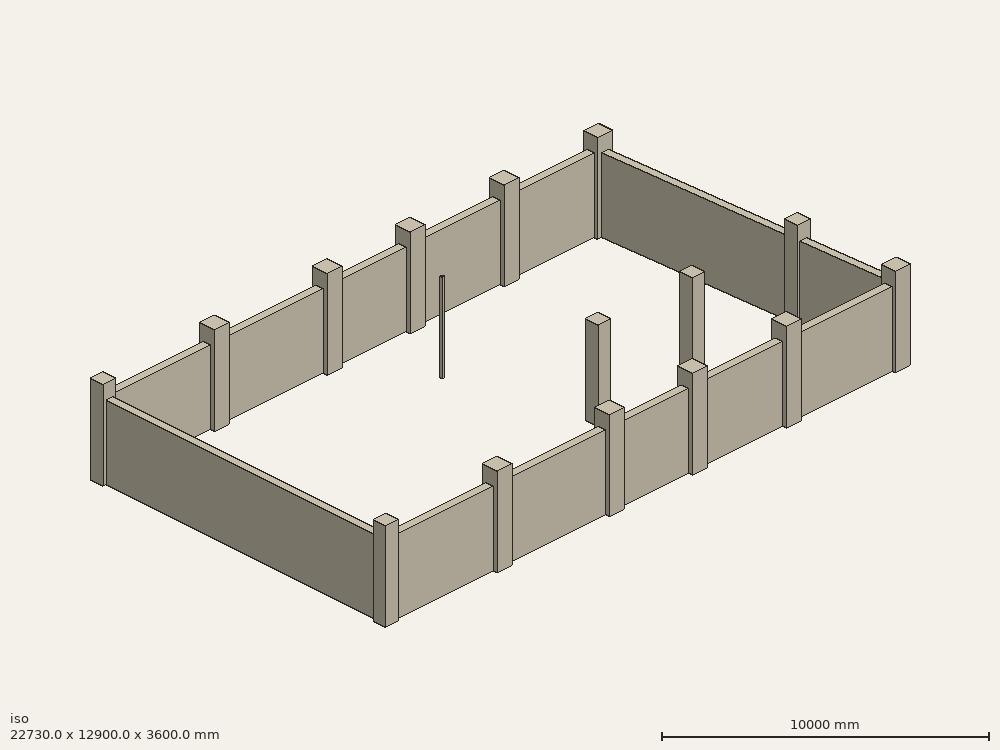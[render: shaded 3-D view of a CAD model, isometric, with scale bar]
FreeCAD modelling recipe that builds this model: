
FCSTD DOCUMENT  (FreeCAD 0.19R24291 (Git))
Label: karimi
License: All rights reserved
LicenseURL: http://en.wikipedia.org/wiki/All_rights_reserved
objects: App::FeaturePython×115, Part::Part2DObjectPython×66, Part::FeaturePython×45, Part::Feature×20, App::DocumentObjectGroup×5, App::DocumentObjectGroupPython×2, App::MaterialObjectPython×1, Fem::ConstraintForce×1
note: 260 computed .brp shape members not serialized (recipe doc carries the construction recipe); baked Part::Feature solids carry a one-line shape summary decoded from their .brp

FEATURE [App::DocumentObjectGroup] Columns
FEATURE [Part::Part2DObjectPython] C65X65_20T25_C40  label="C65X65-20T25_C40"  # Draft 2D object (typed FeaturePython)
  Height = 650
  Width = 650
FEATURE [Part::Part2DObjectPython] C65X65_16T20_C40  label="C65X65-16T20_C40"  # Draft 2D object (typed FeaturePython)
  Height = 650
  Width = 650
FEATURE [Part::Part2DObjectPython] C65X65_16T25_C40  label="C65X65-16T25_C40"  # Draft 2D object (typed FeaturePython)
  Height = 650
  Width = 650
FEATURE [Part::Part2DObjectPython] C55X55_12T25_C40  label="C55X55-12T25_C40"  # Draft 2D object (typed FeaturePython)
  Height = 550
  Width = 550
FEATURE [Part::Part2DObjectPython] C55X55_20T25_C40  label="C55X55-20T25_C40"  # Draft 2D object (typed FeaturePython)
  Height = 550
  Width = 550
FEATURE [Part::Part2DObjectPython] Line026  # Draft 2D object (typed FeaturePython)
  Area = 0
  ChamferSize = 0
  Closed = false
  End = (4790,12260,0)
  FilletRadius = 0
  Length = 12250
  MakeFace = true
  Points = (2) [(4790,10,0),(4790,12260,0)]
  Start = (4790,10,0)
  Subdivisions = 0
  type = Beam
FEATURE [Part::Part2DObjectPython] Line027  # Draft 2D object (typed FeaturePython)
  Area = 0
  ChamferSize = 0
  Closed = false
  End = (21910,4110,0)
  FilletRadius = 0
  Length = 4570
  MakeFace = true
  Points = (2) [(17340,4110,0),(21910,4110,0)]
  Start = (17340,4110,0)
  Subdivisions = 0
  type = Beam
FEATURE [Part::Part2DObjectPython] Line028  # Draft 2D object (typed FeaturePython)
  Area = 0
  ChamferSize = 0
  Closed = false
  End = (17340,4110,0)
  FilletRadius = 0
  Length = 4080
  MakeFace = true
  Points = (2) [(13260,4110,0),(17340,4110,0)]
  Start = (13260,4110,0)
  Subdivisions = 0
  type = Beam
FEATURE [Part::Part2DObjectPython] Line035  # Draft 2D object (typed FeaturePython)
  Area = 0
  ChamferSize = 0
  Closed = false
  End = (9660,12260,0)
  FilletRadius = 0
  Length = 12250
  MakeFace = true
  Points = (2) [(9660,10,0),(9660,12260,0)]
  Start = (9660,10,0)
  Subdivisions = 0
  type = Beam
FEATURE [Part::Part2DObjectPython] Line036  # Draft 2D object (typed FeaturePython)
  Area = 0
  ChamferSize = 0
  Closed = false
  End = (13260,4110,0)
  FilletRadius = 0
  Length = 3600
  MakeFace = true
  Points = (2) [(9660,4110,0),(13260,4110,0)]
  Start = (9660,4110,0)
  Subdivisions = 0
  type = Beam
FEATURE [App::DocumentObjectGroup] Beams
  Group = -> [Line026,Line027,Line028,Line035,Line036]
FEATURE [Part::Part2DObjectPython] BOX10X10  # Draft 2D object (typed FeaturePython)
  Height = 100
  Thickness = 4
  Width = 100
FEATURE [App::FeaturePython] Safe  # WARN: FeaturePython — macro-defined, semantics opaque (R4)
  input = <path>
  input_str = <blob: 95420 chars omitted>
  output = <path>
FEATURE [Part::Part2DObjectPython] Line037  # Draft 2D object (typed FeaturePython)
  Area = 0
  ChamferSize = 0
  Closed = false
  End = (13260,10,0)
  FilletRadius = 0
  Length = 12250
  MakeFace = true
  Points = (2) [(13260,12260,0),(13260,10,0)]
  Start = (13260,12260,0)
  Subdivisions = 0
  type = Beam
FEATURE [Part::Part2DObjectPython] Line038  # Draft 2D object (typed FeaturePython)
  Area = 0
  ChamferSize = 0
  Closed = false
  End = (17340,10,0)
  FilletRadius = 0
  Length = 12250
  MakeFace = true
  Points = (2) [(17340,12260,0),(17340,10,0)]
  Start = (17340,12260,0)
  Subdivisions = 0
  type = Beam
FEATURE [App::FeaturePython] Layer001  label="DIM"  # WARN: FeaturePython — macro-defined, semantics opaque (R4)
FEATURE [App::FeaturePython] Layer002  label="text"  # WARN: FeaturePython — macro-defined, semantics opaque (R4)
FEATURE [App::FeaturePython] Layer003  label="Defpoints"  # WARN: FeaturePython — macro-defined, semantics opaque (R4)
FEATURE [App::FeaturePython] Layer004  label="1"  # WARN: FeaturePython — macro-defined, semantics opaque (R4)
FEATURE [App::FeaturePython] Layer005  label="2"  # WARN: FeaturePython — macro-defined, semantics opaque (R4)
FEATURE [App::FeaturePython] Layer006  label="Furniture"  # WARN: FeaturePython — macro-defined, semantics opaque (R4)
FEATURE [App::FeaturePython] Layer007  label="M"  # WARN: FeaturePython — macro-defined, semantics opaque (R4)
FEATURE [App::FeaturePython] Layer008  label="11"  # WARN: FeaturePython — macro-defined, semantics opaque (R4)
FEATURE [App::FeaturePython] Layer009  label="WALL"  # WARN: FeaturePython — macro-defined, semantics opaque (R4)
FEATURE [App::FeaturePython] Layer010  label="TX"  # WARN: FeaturePython — macro-defined, semantics opaque (R4)
FEATURE [App::FeaturePython] Layer011  label="8"  # WARN: FeaturePython — macro-defined, semantics opaque (R4)
FEATURE [App::FeaturePython] Layer012  label="D"  # WARN: FeaturePython — macro-defined, semantics opaque (R4)
FEATURE [App::FeaturePython] Layer013  label="DIM1"  # WARN: FeaturePython — macro-defined, semantics opaque (R4)
FEATURE [App::FeaturePython] Layer014  label="moble1"  # WARN: FeaturePython — macro-defined, semantics opaque (R4)
FEATURE [App::FeaturePython] Layer015  label="sazeh"  # WARN: FeaturePython — macro-defined, semantics opaque (R4)
FEATURE [App::FeaturePython] Layer016  label="kadr"  # WARN: FeaturePython — macro-defined, semantics opaque (R4)
FEATURE [App::FeaturePython] Layer017  label="3"  # WARN: FeaturePython — macro-defined, semantics opaque (R4)
FEATURE [App::FeaturePython] Layer018  label="$AUDIT-BAD-LAYER"  # WARN: FeaturePython — macro-defined, semantics opaque (R4)
FEATURE [App::FeaturePython] Layer019  label="HS2"  # WARN: FeaturePython — macro-defined, semantics opaque (R4)
FEATURE [App::FeaturePython] Layer020  label="t"  # WARN: FeaturePython — macro-defined, semantics opaque (R4)
FEATURE [App::FeaturePython] Layer021  label="LAYER1"  # WARN: FeaturePython — macro-defined, semantics opaque (R4)
FEATURE [App::FeaturePython] Layer022  label="TXT"  # WARN: FeaturePython — macro-defined, semantics opaque (R4)
FEATURE [App::FeaturePython] Layer023  label="CADR"  # WARN: FeaturePython — macro-defined, semantics opaque (R4)
FEATURE [App::FeaturePython] Layer024  label="Kk"  # WARN: FeaturePython — macro-defined, semantics opaque (R4)
FEATURE [App::FeaturePython] Layer025  label="AR"  # WARN: FeaturePython — macro-defined, semantics opaque (R4)
FEATURE [App::FeaturePython] Layer026  label="kader"  # WARN: FeaturePython — macro-defined, semantics opaque (R4)
FEATURE [App::FeaturePython] Layer027  label="Ar-1"  # WARN: FeaturePython — macro-defined, semantics opaque (R4)
FEATURE [App::FeaturePython] Layer028  label="A-CADRE"  # WARN: FeaturePython — macro-defined, semantics opaque (R4)
FEATURE [App::FeaturePython] Layer029  label="TEXT - 0"  # WARN: FeaturePython — macro-defined, semantics opaque (R4)
FEATURE [App::FeaturePython] Layer030  label="band 3"  # WARN: FeaturePython — macro-defined, semantics opaque (R4)
FEATURE [App::FeaturePython] Layer031  label="PP"  # WARN: FeaturePython — macro-defined, semantics opaque (R4)
FEATURE [App::FeaturePython] Layer032  label="DOOR"  # WARN: FeaturePython — macro-defined, semantics opaque (R4)
FEATURE [App::FeaturePython] Layer033  label="PELEH"  # WARN: FeaturePython — macro-defined, semantics opaque (R4)
FEATURE [App::FeaturePython] Layer034  label="AXE"  # WARN: FeaturePython — macro-defined, semantics opaque (R4)
FEATURE [App::FeaturePython] Layer035  label="HATCH"  # WARN: FeaturePython — macro-defined, semantics opaque (R4)
FEATURE [App::FeaturePython] Layer036  label="DI"  # WARN: FeaturePython — macro-defined, semantics opaque (R4)
FEATURE [App::FeaturePython] Layer037  label="FUR"  # WARN: FeaturePython — macro-defined, semantics opaque (R4)
FEATURE [App::FeaturePython] Layer038  label="HID"  # WARN: FeaturePython — macro-defined, semantics opaque (R4)
FEATURE [App::FeaturePython] Layer039  label="Kit"  # WARN: FeaturePython — macro-defined, semantics opaque (R4)
FEATURE [App::FeaturePython] Layer040  label="win"  # WARN: FeaturePython — macro-defined, semantics opaque (R4)
FEATURE [App::FeaturePython] Layer041  label="HA-WALL"  # WARN: FeaturePython — macro-defined, semantics opaque (R4)
FEATURE [App::FeaturePython] Layer042  label="col2"  # WARN: FeaturePython — macro-defined, semantics opaque (R4)
FEATURE [App::FeaturePython] Layer043  label="DOOR-H"  # WARN: FeaturePython — macro-defined, semantics opaque (R4)
FEATURE [App::FeaturePython] Layer044  label="Stair"  # WARN: FeaturePython — macro-defined, semantics opaque (R4)
FEATURE [App::FeaturePython] Layer045  label="air curtain"  # WARN: FeaturePython — macro-defined, semantics opaque (R4)
FEATURE [App::FeaturePython] Layer046  label="tk"  # WARN: FeaturePython — macro-defined, semantics opaque (R4)
FEATURE [App::FeaturePython] Layer047  label="HIDDEN"  # WARN: FeaturePython — macro-defined, semantics opaque (R4)
FEATURE [App::FeaturePython] Layer049  label="A-DIM-AXIS"  # WARN: FeaturePython — macro-defined, semantics opaque (R4)
FEATURE [App::FeaturePython] Layer050  label="fur1"  # WARN: FeaturePython — macro-defined, semantics opaque (R4)
FEATURE [App::FeaturePython] Layer051  label="MOBL"  # WARN: FeaturePython — macro-defined, semantics opaque (R4)
FEATURE [App::FeaturePython] Layer052  label="W"  # WARN: FeaturePython — macro-defined, semantics opaque (R4)
FEATURE [App::FeaturePython] Layer053  label="H"  # WARN: FeaturePython — macro-defined, semantics opaque (R4)
FEATURE [App::FeaturePython] Layer054  label="FF"  # WARN: FeaturePython — macro-defined, semantics opaque (R4)
FEATURE [App::FeaturePython] Layer055  label="FL"  # WARN: FeaturePython — macro-defined, semantics opaque (R4)
FEATURE [App::FeaturePython] Layer056  label="7"  # WARN: FeaturePython — macro-defined, semantics opaque (R4)
FEATURE [App::FeaturePython] Layer057  label="1."  # WARN: FeaturePython — macro-defined, semantics opaque (R4)
FEATURE [App::FeaturePython] Layer058  label="2."  # WARN: FeaturePython — macro-defined, semantics opaque (R4)
FEATURE [App::FeaturePython] Layer059  label="AM_0"  # WARN: FeaturePython — macro-defined, semantics opaque (R4)
FEATURE [App::FeaturePython] Layer060  label="A-PROFILE"  # WARN: FeaturePython — macro-defined, semantics opaque (R4)
FEATURE [App::FeaturePython] Layer061  label="A-DOOR"  # WARN: FeaturePython — macro-defined, semantics opaque (R4)
FEATURE [App::FeaturePython] Layer062  label="A-STAIR"  # WARN: FeaturePython — macro-defined, semantics opaque (R4)
FEATURE [App::FeaturePython] Layer063  label="WINDOW"  # WARN: FeaturePython — macro-defined, semantics opaque (R4)
FEATURE [App::FeaturePython] Layer064  label="PUERTAS"  # WARN: FeaturePython — macro-defined, semantics opaque (R4)
FEATURE [App::FeaturePython] Layer065  label="FURN"  # WARN: FeaturePython — macro-defined, semantics opaque (R4)
FEATURE [App::FeaturePython] Layer066  label="251"  # WARN: FeaturePython — macro-defined, semantics opaque (R4)
FEATURE [App::FeaturePython] Layer067  label="FURNITURE-SERVICE"  # WARN: FeaturePython — macro-defined, semantics opaque (R4)
FEATURE [App::FeaturePython] Layer068  label="NO PRINT"  # WARN: FeaturePython — macro-defined, semantics opaque (R4)
FEATURE [App::FeaturePython] Layer069  label="67"  # WARN: FeaturePython — macro-defined, semantics opaque (R4)
FEATURE [App::FeaturePython] Layer070  label="mobleman .1"  # WARN: FeaturePython — macro-defined, semantics opaque (R4)
FEATURE [App::FeaturePython] Layer071  label="Frame"  # WARN: FeaturePython — macro-defined, semantics opaque (R4)
FEATURE [App::FeaturePython] Layer072  label="carros"  # WARN: FeaturePython — macro-defined, semantics opaque (R4)
FEATURE [App::FeaturePython] Layer073  label="MUEBLES"  # WARN: FeaturePython — macro-defined, semantics opaque (R4)
FEATURE [App::FeaturePython] Layer074  label="NOI THAT"  # WARN: FeaturePython — macro-defined, semantics opaque (R4)
FEATURE [App::FeaturePython] Layer075  label="B-FURNITURE"  # WARN: FeaturePython — macro-defined, semantics opaque (R4)
FEATURE [App::FeaturePython] Layer076  label="nazok kary"  # WARN: FeaturePython — macro-defined, semantics opaque (R4)
FEATURE [App::FeaturePython] Layer077  label="mobiliarios"  # WARN: FeaturePython — macro-defined, semantics opaque (R4)
FEATURE [App::FeaturePython] Layer078  label="moveis"  # WARN: FeaturePython — macro-defined, semantics opaque (R4)
FEATURE [App::FeaturePython] Layer079  label="PLANTAS"  # WARN: FeaturePython — macro-defined, semantics opaque (R4)
FEATURE [App::FeaturePython] Layer080  label="PROIEZIONI"  # WARN: FeaturePython — macro-defined, semantics opaque (R4)
FEATURE [App::FeaturePython] Layer081  label="NEMA"  # WARN: FeaturePython — macro-defined, semantics opaque (R4)
FEATURE [App::FeaturePython] Layer082  label="facade"  # WARN: FeaturePython — macro-defined, semantics opaque (R4)
FEATURE [App::FeaturePython] Layer083  label="khat chin"  # WARN: FeaturePython — macro-defined, semantics opaque (R4)
FEATURE [App::FeaturePython] Layer084  label="A-FURNITURE"  # WARN: FeaturePython — macro-defined, semantics opaque (R4)
FEATURE [App::FeaturePython] Layer085  label="NIVO"  # WARN: FeaturePython — macro-defined, semantics opaque (R4)
FEATURE [App::FeaturePython] Layer086  label="ext-wall"  # WARN: FeaturePython — macro-defined, semantics opaque (R4)
FEATURE [App::FeaturePython] Layer087  label="stairs"  # WARN: FeaturePython — macro-defined, semantics opaque (R4)
FEATURE [App::FeaturePython] Layer088  label="Plot-TEXT-2"  # WARN: FeaturePython — macro-defined, semantics opaque (R4)
FEATURE [App::FeaturePython] Layer089  label="A-AXIS"  # WARN: FeaturePython — macro-defined, semantics opaque (R4)
FEATURE [App::FeaturePython] Layer090  label="int-wall"  # WARN: FeaturePython — macro-defined, semantics opaque (R4)
FEATURE [App::FeaturePython] Layer091  label="STAIR2"  # WARN: FeaturePython — macro-defined, semantics opaque (R4)
FEATURE [App::FeaturePython] Layer092  label="kadr 2"  # WARN: FeaturePython — macro-defined, semantics opaque (R4)
FEATURE [App::FeaturePython] Layer093  label="WIN FACAD"  # WARN: FeaturePython — macro-defined, semantics opaque (R4)
FEATURE [App::FeaturePython] Layer094  label="win1"  # WARN: FeaturePython — macro-defined, semantics opaque (R4)
FEATURE [App::FeaturePython] Layer095  label="javab5"  # WARN: FeaturePython — macro-defined, semantics opaque (R4)
FEATURE [App::FeaturePython] Layer096  label="99"  # WARN: FeaturePython — macro-defined, semantics opaque (R4)
FEATURE [App::FeaturePython] Layer097  label="A-SECTION"  # WARN: FeaturePython — macro-defined, semantics opaque (R4)
FEATURE [App::FeaturePython] Layer098  label="a"  # WARN: FeaturePython — macro-defined, semantics opaque (R4)
FEATURE [Part::Feature] Line039
  shape: bbox 5774 x 11470 x 2e-07 mm, 0 faces, 0 solids (baked)
FEATURE [App::FeaturePython] Layer048  label="A-WALL"  # WARN: FeaturePython — macro-defined, semantics opaque (R4)
  Group = -> [Line039]
FEATURE [Part::Feature] Line040
  shape: bbox 22090 x 2e-07 x 2e-07 mm, 0 faces, 0 solids (baked)
FEATURE [Part::Feature] Line041
  shape: bbox 710 x 13000 x 2e-07 mm, 0 faces, 0 solids (baked)
FEATURE [Part::Feature] Line042
  shape: bbox 22800 x 2e-07 x 2e-07 mm, 0 faces, 0 solids (baked)
FEATURE [Part::Feature] Line043
  shape: bbox 2e-07 x 13000 x 2e-07 mm, 0 faces, 0 solids (baked)
FEATURE [Part::Feature] Block_fghfhfhg
  Placement = pos=(21402.7,12250,0) rot=(0,0,1;0rad)
  shape: bbox 875 x 875 x 2e-07 mm, 2 faces, 0 solids (baked)
FEATURE [Part::Feature] Block_fghfhfhg001
  Placement = pos=(9650,12250,0) rot=(0,0,1;0rad)
  shape: bbox 875 x 875 x 2e-07 mm, 2 faces, 0 solids (baked)
FEATURE [Part::Feature] Block_fghfhfhg002
  Placement = pos=(13250,12250,0) rot=(0,0,1;0rad)
  shape: bbox 875 x 875 x 2e-07 mm, 2 faces, 0 solids (baked)
FEATURE [Part::Feature] Block_fghfhfhg003
  Placement = pos=(17326.4,12250,0) rot=(0,0,1;0rad)
  shape: bbox 875 x 875 x 2e-07 mm, 2 faces, 0 solids (baked)
FEATURE [Part::Feature] Block_fghfhfhg004
  Placement = pos=(22071.6,0,0) rot=(0,0,1;0rad)
  shape: bbox 875 x 875 x 2e-07 mm, 2 faces, 0 solids (baked)
FEATURE [Part::Feature] Block_fghfhfhg005
  Placement = pos=(21898.8,4100,0) rot=(0,0,1;0rad)
  shape: bbox 875 x 875 x 2e-07 mm, 2 faces, 0 solids (baked)
FEATURE [Part::Feature] Block_fghfhfhg006
  Placement = pos=(17324.6,4100,0) rot=(0,0,1;0rad)
  shape: bbox 875 x 875 x 2e-07 mm, 2 faces, 0 solids (baked)
FEATURE [Part::Feature] Block_fghfhfhg007
  Placement = pos=(9650,0,0) rot=(0,0,1;0rad)
  shape: bbox 875 x 875 x 2e-07 mm, 2 faces, 0 solids (baked)
FEATURE [Part::Feature] Block_fghfhfhg008
  Placement = pos=(13250,0,0) rot=(0,0,1;0rad)
  shape: bbox 875 x 875 x 2e-07 mm, 2 faces, 0 solids (baked)
FEATURE [Part::Feature] Block_fghfhfhg009
  Placement = pos=(17326.4,0,0) rot=(0,0,1;0rad)
  shape: bbox 875 x 875 x 2e-07 mm, 2 faces, 0 solids (baked)
FEATURE [Part::Feature] Block_fghfhfhg010
  Placement = pos=(13248.2,4100,0) rot=(0,0,1;0rad)
  shape: bbox 875 x 875 x 2e-07 mm, 2 faces, 0 solids (baked)
FEATURE [Part::Feature] Block_sdfasdgfghfghtrtht
  Placement = pos=(-231196,-37243.3,0) rot=(0,0,1;0rad)
  shape: bbox 975 x 875 x 2e-07 mm, 2 faces, 0 solids (baked)
FEATURE [Part::Feature] Block_sdfasdgfghfghtrtht001
  Placement = pos=(-231196,-24993.3,0) rot=(0,0,1;0rad)
  shape: bbox 975 x 875 x 2e-07 mm, 2 faces, 0 solids (baked)
FEATURE [Part::Feature] Block_fghfhfhg011
  shape: bbox 875 x 875 x 2e-07 mm, 2 faces, 0 solids (baked)
FEATURE [Part::Feature] Block_fghfhfhg012
  Placement = pos=(0,12250,0) rot=(0,0,1;0rad)
  shape: bbox 875 x 875 x 2e-07 mm, 2 faces, 0 solids (baked)
FEATURE [App::FeaturePython] Layer  label="0"  # WARN: FeaturePython — macro-defined, semantics opaque (R4)
  Group = -> [Line040,Line041,Line042,Line043,Block_fghfhfhg,Block_fghfhfhg001,Block_fghfhfhg002,Block_fghfhfhg003,Block_fghfhfhg004,Block_fghfhfhg005,Block_fghfhfhg006,Block_fghfhfhg007,Block_fghfhfhg008,Block_fghfhfhg009,Block_fghfhfhg010,Block_sdfasdgfghfghtrtht,Block_sdfasdgfghfghtrtht001,Block_fghfhfhg011,Block_fghfhfhg012]
FEATURE [App::DocumentObjectGroupPython] LayerContainer  label="Layers"  # scripted group (container) (typed FeaturePython)
  Group = -> [Layer018,Layer,Layer004,Layer057,Layer008,Layer005,Layer058,Layer066,Layer017,Layer069,Layer056,Layer011,Layer096,Layer089,Layer028,Layer049,Layer061,Layer084,Layer060,Layer097,Layer062,Layer048,Layer059,Layer025,Layer034,Layer027,Layer075,Layer023,Layer012,Layer036,Layer001,Layer013,Layer032,Layer043,Layer003,Layer054,Layer055,Layer037,Layer065,Layer067,Layer071,Layer006,Layer053,Layer041,+55 more]
FEATURE [Part::Part2DObjectPython] Line048  # Draft 2D object (typed FeaturePython)
  Area = 0
  ChamferSize = 0
  Closed = false
  End = (4790,12260,0)
  FilletRadius = 0
  Length = 12250
  MakeFace = false
  Points = (2) [(4790,10,0),(4790,12260,0)]
  Start = (4790,10,0)
  Subdivisions = 0
FEATURE [Part::FeaturePython] BaseFoundation  # Arch/BIM 77 (typed FeaturePython)
  Base = -> Line048
  HorizontalArea = 0
  IfcData = attributes={"GlobalId": {"name": "GlobalId", "type": "IfcGloballyUniqueId", "is_enum": false, "enum_values": []}, "Description": {"... (+511 chars omitted),+1 more (map truncated)
  IfcType = 77
  MoveBase = false
  MoveWithHost = false
  PerimeterLength = 0
  PredefinedType = 0
  VerticalArea = 0
  align = 0
  design_type = 0
  fc = 25000
  final_wire_first_point = (0,0,0)
  final_wire_last_point = (0,0,0)
  height = 1000
  ks = 3
  layer = 1
  left_width = 500
  right_width = 500
  width = 1000
  expr: ks = -2.2 * .width.Value / 1000 + 5.2
FEATURE [Part::Part2DObjectPython] Wire  # Draft 2D object (typed FeaturePython)
  Area = 0
  ChamferSize = 0
  Closed = false
  End = (21910,4110,0)
  FilletRadius = 0
  Length = 8650
  MakeFace = false
  Points = (3) [(13260,4110,0),(17340,4110,0),(21910,4110,0)]
  Start = (13260,4110,0)
  Subdivisions = 0
FEATURE [Part::FeaturePython] BaseFoundation006  # Arch/BIM 77 (typed FeaturePython)
  Base = -> Wire
  HorizontalArea = 0
  IfcData = attributes={"GlobalId": {"name": "GlobalId", "type": "IfcGloballyUniqueId", "is_enum": false, "enum_values": []}, "Description": {"... (+511 chars omitted),+1 more (map truncated)
  IfcType = 77
  MoveBase = false
  MoveWithHost = false
  PerimeterLength = 0
  PredefinedType = 0
  VerticalArea = 0
  align = 0
  design_type = 0
  fc = 25000
  final_wire_first_point = (0,0,0)
  final_wire_last_point = (0,0,0)
  height = 700
  ks = 3.66
  layer = 0
  left_width = 350
  right_width = 350
  width = 700
  expr: ks = -2.2 * .width.Value / 1000 + 5.2
FEATURE [Part::Part2DObjectPython] Line050  # Draft 2D object (typed FeaturePython)
  Area = 0
  ChamferSize = 0
  Closed = false
  End = (13260,10,0)
  FilletRadius = 0
  Length = 12250
  MakeFace = false
  Points = (2) [(13260,12260,0),(13260,10,0)]
  Start = (13260,12260,0)
  Subdivisions = 0
FEATURE [Part::FeaturePython] BaseFoundation007  # Arch/BIM 77 (typed FeaturePython)
  Base = -> Line050
  HorizontalArea = 0
  IfcData = attributes={"GlobalId": {"name": "GlobalId", "type": "IfcGloballyUniqueId", "is_enum": false, "enum_values": []}, "Description": {"... (+511 chars omitted),+1 more (map truncated)
  IfcType = 77
  MoveBase = false
  MoveWithHost = false
  PerimeterLength = 0
  PredefinedType = 0
  VerticalArea = 0
  align = 0
  design_type = 0
  fc = 25000
  final_wire_first_point = (0,0,0)
  final_wire_last_point = (0,0,0)
  height = 1000
  ks = 3
  layer = 1
  left_width = 500
  right_width = 500
  width = 1000
  expr: ks = -2.2 * .width.Value / 1000 + 5.2
FEATURE [Part::Part2DObjectPython] Line052  # Draft 2D object (typed FeaturePython)
  Area = 0
  ChamferSize = 0
  Closed = false
  End = (21764.9,12625,0)
  FilletRadius = 0
  Length = 22089.9
  MakeFace = false
  Points = (2) [(-325,12625,0),(21764.9,12625,0)]
  Start = (-325,12625,0)
  Subdivisions = 0
FEATURE [Part::Part2DObjectPython] Line053  # Draft 2D object (typed FeaturePython)
  Area = 0
  ChamferSize = 0
  Closed = false
  End = (-325,-375,0)
  FilletRadius = 0
  Length = 22800
  MakeFace = false
  Points = (2) [(22475,-375,0),(-325,-375,0)]
  Start = (22475,-375,0)
  Subdivisions = 0
FEATURE [Part::Part2DObjectPython] Line054  # Draft 2D object (typed FeaturePython)
  Area = 0
  ChamferSize = 0
  Closed = false
  End = (22475,-375,0)
  FilletRadius = 0
  Length = 13019.4
  MakeFace = false
  Points = (2) [(21765,12625,0),(22475,-375,0)]
  Start = (21765,12625,0)
  Subdivisions = 0
FEATURE [Part::Part2DObjectPython] Line055  # Draft 2D object (typed FeaturePython)
  Area = 0
  ChamferSize = 0
  Closed = false
  End = (-325,12625,0)
  FilletRadius = 0
  Length = 13000
  MakeFace = false
  Points = (2) [(-325,-375,0),(-325,12625,0)]
  Start = (-325,-375,0)
  Subdivisions = 0
FEATURE [Part::Part2DObjectPython] Line056  # Draft 2D object (typed FeaturePython)
  Area = 0
  ChamferSize = 0
  Closed = false
  End = (4790,12625,0)
  FilletRadius = 0
  Length = 13000
  MakeFace = false
  Points = (2) [(4790,-375,0),(4790,12625,0)]
  Start = (4790,-375,0)
  Subdivisions = 0
FEATURE [Part::Part2DObjectPython] Line057  # Draft 2D object (typed FeaturePython)
  Area = 0
  ChamferSize = 0
  Closed = false
  End = (9660,12625,0)
  FilletRadius = 0
  Length = 13000
  MakeFace = false
  Points = (2) [(9660,-375,0),(9660,12625,0)]
  Start = (9660,-375,0)
  Subdivisions = 0
FEATURE [Part::Part2DObjectPython] Line058  # Draft 2D object (typed FeaturePython)
  Area = 0
  ChamferSize = 0
  Closed = false
  End = (22230,4110,0)
  FilletRadius = 0
  Length = 13170
  MakeFace = false
  Points = (2) [(9060,4110,0),(22230,4110,0)]
  Start = (9060,4110,0)
  Subdivisions = 0
FEATURE [Part::Part2DObjectPython] Line059  # Draft 2D object (typed FeaturePython)
  Area = 0
  ChamferSize = 0
  Closed = false
  End = (13260,-375,0)
  FilletRadius = 0
  Length = 13000
  MakeFace = false
  Points = (2) [(13260,12625,0),(13260,-375,0)]
  Start = (13260,12625,0)
  Subdivisions = 0
FEATURE [Part::Part2DObjectPython] Line060  # Draft 2D object (typed FeaturePython)
  Area = 0
  ChamferSize = 0
  Closed = false
  End = (17340,-375,0)
  FilletRadius = 0
  Length = 13000
  MakeFace = false
  Points = (2) [(17340,12625,0),(17340,-375,0)]
  Start = (17340,12625,0)
  Subdivisions = 0
FEATURE [Part::Part2DObjectPython] C60X65_14T20_C40  label="C60X65-14T20_C40"  # Draft 2D object (typed FeaturePython)
  Height = 650
  Width = 600
FEATURE [Part::Part2DObjectPython] C65X65_20T25_C041  label="C65X65-20T25_C041"  # Draft 2D object (typed FeaturePython)
  Height = 650
  Width = 650
FEATURE [Part::Part2DObjectPython] C65X65_16T20_C041  label="C65X65-16T20_C041"  # Draft 2D object (typed FeaturePython)
  Height = 650
  Width = 650
FEATURE [Part::Part2DObjectPython] C65X65_16T25_C041  label="C65X65-16T25_C041"  # Draft 2D object (typed FeaturePython)
  Height = 650
  Width = 650
FEATURE [Part::Part2DObjectPython] C55X55_12T25_C041  label="C55X55-12T25_C041"  # Draft 2D object (typed FeaturePython)
  Height = 550
  Width = 550
FEATURE [Part::Part2DObjectPython] BOX10X011  # Draft 2D object (typed FeaturePython)
  Height = 100
  Thickness = 4
  Width = 100
FEATURE [Part::Part2DObjectPython] C55X55_20T25_C041  label="C55X55-20T25_C041"  # Draft 2D object (typed FeaturePython)
  Height = 550
  Width = 550
FEATURE [Part::Part2DObjectPython] Wire001  # Draft 2D object (typed FeaturePython)
  Area = 0
  ChamferSize = 0
  Closed = false
  End = (10,12260,0)
  FilletRadius = 0
  Length = 12250
  MakeFace = true
  Points = (3) [(10,10,0),(10,12260,0),(10,12260,0)]
  Start = (10,10,0)
  Subdivisions = 0
FEATURE [Part::FeaturePython] BaseFoundation010  # Arch/BIM 77 (typed FeaturePython)
  Base = -> Wire001
  HorizontalArea = 0
  IfcData = attributes={"GlobalId": {"name": "GlobalId", "type": "IfcGloballyUniqueId", "is_enum": false, "enum_values": []}, "Description": {"... (+511 chars omitted),+1 more (map truncated)
  IfcType = 77
  MoveBase = false
  MoveWithHost = false
  PerimeterLength = 0
  PredefinedType = 0
  VerticalArea = 0
  align = 1
  design_type = 0
  fc = 30000
  final_wire_first_point = (0,0,0)
  final_wire_last_point = (0,0,0)
  height = 700
  ks = 3.66
  layer = 1
  left_width = 280
  right_width = 420
  width = 700
  expr: ks = -2.2 * .width.Value / 1000 + 5.2
FEATURE [Part::Part2DObjectPython] Line061  # Draft 2D object (typed FeaturePython)
  Area = 0
  ChamferSize = 0
  Closed = false
  End = (22140,10,0)
  FilletRadius = 0
  Length = 12267.8
  MakeFace = true
  Points = (2) [(21480,12260,0),(22140,10,0)]
  Start = (21480,12260,0)
  Subdivisions = 0
FEATURE [Part::FeaturePython] BaseFoundation012  # Arch/BIM 77 (typed FeaturePython)
  Base = -> Line061
  HorizontalArea = 0
  IfcData = attributes={"GlobalId": {"name": "GlobalId", "type": "IfcGloballyUniqueId", "is_enum": false, "enum_values": []}, "Description": {"... (+511 chars omitted),+1 more (map truncated)
  IfcType = 77
  MoveBase = false
  MoveWithHost = false
  PerimeterLength = 0
  PredefinedType = 0
  VerticalArea = 0
  align = 1
  design_type = 0
  fc = 30000
  final_wire_first_point = (0,0,0)
  final_wire_last_point = (0,0,0)
  height = 1000
  ks = 3
  layer = 1
  left_width = 350
  right_width = 650
  width = 1000
  expr: ks = -2.2 * .width.Value / 1000 + 5.2
FEATURE [Part::Part2DObjectPython] Line062  # Draft 2D object (typed FeaturePython)
  Area = 0
  ChamferSize = 0
  Closed = true
  End = (4790,10,0)
  FilletRadius = 0
  Length = 17350
  MakeFace = true
  Points = (2) [(22140,10,0),(4790,10,0)]
  Start = (22140,10,0)
  Subdivisions = 0
FEATURE [Part::FeaturePython] BaseFoundation016  # Arch/BIM 77 (typed FeaturePython)
  Base = -> Line062
  HorizontalArea = 0
  IfcData = attributes={"GlobalId": {"name": "GlobalId", "type": "IfcGloballyUniqueId", "is_enum": false, "enum_values": []}, "Description": {"... (+511 chars omitted),+1 more (map truncated)
  IfcType = 77
  MoveBase = false
  MoveWithHost = false
  PerimeterLength = 0
  PredefinedType = 0
  VerticalArea = 0
  align = 1
  design_type = 0
  fc = 30000
  final_wire_first_point = (0,0,0)
  final_wire_last_point = (0,0,0)
  height = 900
  ks = 1.46
  layer = 0
  left_width = 380
  right_width = 1320
  width = 1700
  expr: ks = -2.2 * .width.Value / 1000 + 5.2
FEATURE [Part::Part2DObjectPython] Line063  # Draft 2D object (typed FeaturePython)
  Area = 0
  ChamferSize = 0
  Closed = true
  End = (9845,9340,0)
  FilletRadius = 0
  Length = 3415
  MakeFace = true
  Points = (2) [(13260,9340,0),(9845,9340,0)]
  Start = (13260,9340,0)
  Subdivisions = 0
FEATURE [Part::FeaturePython] BaseFoundation018  # Arch/BIM 77 (typed FeaturePython)
  Base = -> Line063
  HorizontalArea = 0
  IfcData = attributes={"GlobalId": {"name": "GlobalId", "type": "IfcGloballyUniqueId", "is_enum": false, "enum_values": []}, "Description": {"... (+511 chars omitted),+1 more (map truncated)
  IfcType = 77
  MoveBase = false
  MoveWithHost = false
  PerimeterLength = 0
  PredefinedType = 0
  VerticalArea = 0
  align = 1
  design_type = 0
  fc = 30000
  final_wire_first_point = (0,0,0)
  final_wire_last_point = (0,0,0)
  height = 600
  ks = 3.88
  layer = 0
  left_width = 50
  right_width = 550
  width = 600
  expr: ks = -2.2 * .width.Value / 1000 + 5.2
FEATURE [Part::Part2DObjectPython] Line064  # Draft 2D object (typed FeaturePython)
  Area = 0
  ChamferSize = 0
  Closed = false
  End = (21155,12260,0)
  FilletRadius = 0
  Length = 20870
  MakeFace = true
  Points = (2) [(285,12260,0),(21155,12260,0)]
  Start = (285,12260,0)
  Subdivisions = 0
  type = Beam
FEATURE [Part::Part2DObjectPython] Line065  # Draft 2D object (typed FeaturePython)
  Area = 0
  ChamferSize = 0
  Closed = false
  End = (22140,310,0)
  FilletRadius = 0
  Length = 11668.7
  MakeFace = true
  Points = (2) [(21480,11960,0),(22140,310,0)]
  Start = (21480,11960,0)
  Subdivisions = 0
  type = Beam
FEATURE [Part::Part2DObjectPython] Line066  # Draft 2D object (typed FeaturePython)
  Area = 0
  ChamferSize = 0
  Closed = false
  End = (285,10,0)
  FilletRadius = 0
  Length = 21530
  MakeFace = true
  Points = (2) [(21815,10,0),(285,10,0)]
  Start = (21815,10,0)
  Subdivisions = 0
  type = Beam
FEATURE [Part::Part2DObjectPython] Line067  # Draft 2D object (typed FeaturePython)
  Area = 0
  ChamferSize = 0
  Closed = false
  End = (10,11985,0)
  FilletRadius = 0
  Length = 11700
  MakeFace = true
  Points = (2) [(10,285,0),(10,11985,0)]
  Start = (10,285,0)
  Subdivisions = 0
  type = Beam
FEATURE [App::MaterialObjectPython] Bricks  # material (typed FeaturePython)
  Material = DiffuseColor=(0.8899999856948853, 0.8899999856948853, 0.0); Name=Bricks; SectionColor=(0.0, 0.0, 0.0); Transparency=0
  Transparency = 0
FEATURE [App::DocumentObjectGroupPython] MaterialContainer  label="Materials"  # scripted group (container) (typed FeaturePython)
  Group = -> [Bricks]
FEATURE [Part::FeaturePython] Wall  # Arch/BIM 166 (typed FeaturePython)
  Align = 2
  Area = 35100000
  Base = -> Line067
  BlockHeight = 0
  BlockLength = 0
  CountBroken = 0
  CountEntire = 0
  Face = 0
  Height = 3000
  HorizontalArea = 3510000
  IfcData = attributes={"GlobalId": {"name": "GlobalId", "type": "IfcGloballyUniqueId", "is_enum": false, "enum_values": []}, "Description": {"... (+533 chars omitted),+1 more (map truncated)
  IfcType = 166
  Joint = 0
  Length = 11700
  MakeBlocks = false
  Material = -> Bricks
  MoveBase = false
  MoveWithHost = false
  Normal = (0,0,0)
  OffsetFirst = 0
  OffsetSecond = 0
  PerimeterLength = 24000
  PredefinedType = 0
  VerticalArea = 72000000
  Width = 300
  loadpat = DL
  weight = 300
FEATURE [Part::FeaturePython] Wall001  # Arch/BIM 166 (typed FeaturePython)
  Align = 2
  Area = 62610000
  Base = -> Line064
  BlockHeight = 0
  BlockLength = 0
  CountBroken = 0
  CountEntire = 0
  Face = 0
  Height = 3000
  HorizontalArea = 6261000
  IfcData = attributes={"GlobalId": {"name": "GlobalId", "type": "IfcGloballyUniqueId", "is_enum": false, "enum_values": []}, "Description": {"... (+533 chars omitted),+1 more (map truncated)
  IfcType = 166
  Joint = 0
  Length = 20870
  MakeBlocks = false
  Material = -> Bricks
  MoveBase = false
  MoveWithHost = false
  Normal = (0,0,0)
  OffsetFirst = 0
  OffsetSecond = 0
  PerimeterLength = 42340
  PredefinedType = 0
  VerticalArea = 127020000
  Width = 300
  loadpat = DL
  weight = 300
FEATURE [Part::FeaturePython] Wall002  # Arch/BIM 166 (typed FeaturePython)
  Align = 2
  Area = 3.5006e+07
  Base = -> Line065
  BlockHeight = 0
  BlockLength = 0
  CountBroken = 0
  CountEntire = 0
  Face = 0
  Height = 3000
  HorizontalArea = 3.5006e+06
  IfcData = attributes={"GlobalId": {"name": "GlobalId", "type": "IfcGloballyUniqueId", "is_enum": false, "enum_values": []}, "Description": {"... (+533 chars omitted),+1 more (map truncated)
  IfcType = 166
  Joint = 0
  Length = 11668.7
  MakeBlocks = false
  Material = -> Bricks
  MoveBase = false
  MoveWithHost = false
  Normal = (0,0,0)
  OffsetFirst = 0
  OffsetSecond = 0
  PerimeterLength = 23937.4
  PredefinedType = 0
  VerticalArea = 7.18121e+07
  Width = 300
  loadpat = DL
  weight = 300
FEATURE [Part::FeaturePython] Wall003  # Arch/BIM 166 (typed FeaturePython)
  Align = 2
  Area = 64590000
  Base = -> Line066
  BlockHeight = 0
  BlockLength = 0
  CountBroken = 0
  CountEntire = 0
  Face = 0
  Height = 3000
  HorizontalArea = 6459000
  IfcData = attributes={"GlobalId": {"name": "GlobalId", "type": "IfcGloballyUniqueId", "is_enum": false, "enum_values": []}, "Description": {"... (+533 chars omitted),+1 more (map truncated)
  IfcType = 166
  Joint = 0
  Length = 21530
  MakeBlocks = false
  Material = -> Bricks
  MoveBase = false
  MoveWithHost = false
  Normal = (0,0,0)
  OffsetFirst = 0
  OffsetSecond = 0
  PerimeterLength = 43660
  PredefinedType = 0
  VerticalArea = 130980000
  Width = 300
  loadpat = DL
  weight = 300
FEATURE [Part::Part2DObjectPython] Wire002  # Draft 2D object (typed FeaturePython)
  Area = 0
  ChamferSize = 0
  Closed = false
  End = (21480,12260,0)
  FilletRadius = 0
  Length = 16690
  MakeFace = true
  Points = (3) [(4790,12260,0),(21480,12260,0),(21480,12260,0)]
  Start = (4790,12260,0)
  Subdivisions = 0
FEATURE [Part::FeaturePython] BaseFoundation020  # Arch/BIM 77 (typed FeaturePython)
  Base = -> Wire002
  HorizontalArea = 0
  IfcData = attributes={"GlobalId": {"name": "GlobalId", "type": "IfcGloballyUniqueId", "is_enum": false, "enum_values": []}, "Description": {"... (+511 chars omitted),+1 more (map truncated)
  IfcType = 77
  MoveBase = false
  MoveWithHost = false
  PerimeterLength = 0
  PredefinedType = 0
  VerticalArea = 0
  align = 1
  design_type = 0
  fc = 30000
  final_wire_first_point = (0,0,0)
  final_wire_last_point = (0,0,0)
  height = 900
  ks = 1.46
  layer = 0
  left_width = 380
  right_width = 1320
  width = 1700
  expr: ks = -2.2 * .width.Value / 1000 + 5.2
FEATURE [Part::Part2DObjectPython] Line068  # Draft 2D object (typed FeaturePython)
  Area = 0
  ChamferSize = 0
  Closed = false
  End = (4790,12260,0)
  FilletRadius = 0
  Length = 4780
  MakeFace = true
  Points = (2) [(10,12260,0),(4790,12260,0)]
  Start = (10,12260,0)
  Subdivisions = 0
FEATURE [Part::FeaturePython] BaseFoundation022  # Arch/BIM 77 (typed FeaturePython)
  Base = -> Line068
  HorizontalArea = 0
  IfcData = attributes={"GlobalId": {"name": "GlobalId", "type": "IfcGloballyUniqueId", "is_enum": false, "enum_values": []}, "Description": {"... (+511 chars omitted),+1 more (map truncated)
  IfcType = 77
  MoveBase = false
  MoveWithHost = false
  PerimeterLength = 0
  PredefinedType = 0
  VerticalArea = 0
  align = 1
  design_type = 0
  fc = 30000
  final_wire_first_point = (0,0,0)
  final_wire_last_point = (0,0,0)
  height = 900
  ks = 3
  layer = 0
  left_width = 380
  right_width = 620
  width = 1000
  expr: ks = -2.2 * .width.Value / 1000 + 5.2
FEATURE [Part::Part2DObjectPython] Line069  # Draft 2D object (typed FeaturePython)
  Area = 0
  ChamferSize = 0
  Closed = false
  End = (10,10,0)
  FilletRadius = 0
  Length = 4780
  MakeFace = true
  Points = (2) [(4790,10,0),(10,10,0)]
  Start = (4790,10,0)
  Subdivisions = 0
FEATURE [Part::FeaturePython] BaseFoundation024  # Arch/BIM 77 (typed FeaturePython)
  Base = -> Line069
  HorizontalArea = 0
  IfcData = attributes={"GlobalId": {"name": "GlobalId", "type": "IfcGloballyUniqueId", "is_enum": false, "enum_values": []}, "Description": {"... (+511 chars omitted),+1 more (map truncated)
  IfcType = 77
  MoveBase = false
  MoveWithHost = false
  PerimeterLength = 0
  PredefinedType = 0
  VerticalArea = 0
  align = 1
  design_type = 0
  fc = 30000
  final_wire_first_point = (0,0,0)
  final_wire_last_point = (0,0,0)
  height = 900
  ks = 3
  layer = 0
  left_width = 380
  right_width = 620
  width = 1000
  expr: ks = -2.2 * .width.Value / 1000 + 5.2
FEATURE [Part::FeaturePython] Foundation  # Arch/BIM 77 (typed FeaturePython)
  HorizontalArea = 0
  IfcType = 77
  MoveBase = false
  MoveWithHost = false
  PerimeterLength = 0
  VerticalArea = 0
  base_foundations = -> [BaseFoundation,BaseFoundation006,BaseFoundation007,BaseFoundation010,BaseFoundation012,BaseFoundation016,BaseFoundation018,BaseFoundation020,BaseFoundation022,BaseFoundation024]
  continuous_layer = 0
  cover = 75
  d = 825
  fc = 30000
  foundation_type = 0
  height = 0
  height_punch = 900
  ks = 2
  level = 0
  redraw = false
  split = true
  tolerance = 0.01
  volume = 103.769
FEATURE [Fem::ConstraintForce] DL
  DirectionVector = (0,0,-1)
  Force = 540
  NormalDirection = (0,0,1)
  Points = (641) [(4290,630,0),(4623.33,630,0),(4956.67,630,0),(5290,630,0),(4290,1277.65,0),(4623.33,1277.65,0),(4956.67,1277.65,0),(5290,1277.65,0),(4290,1925.29,0),+632 more]
  References = -> [Foundation]
  Reversed = true
  Scale = 53
  loadcase = DL
FEATURE [App::DocumentObjectGroup] Beams001
FEATURE [Part::Part2DObjectPython] C65X65_16T20_C042  label="C65X65-16T20_C042"  # Draft 2D object (typed FeaturePython)
  Height = 650
  Width = 650
FEATURE [App::FeaturePython] Safe001  # WARN: FeaturePython — macro-defined, semantics opaque (R4)
  input = <path>
  output = <path>
FEATURE [Part::Part2DObjectPython] Line001  label="C6_GF_CenterLine"  # Draft 2D object (typed FeaturePython)
  Area = 0
  ChamferSize = 0
  Closed = false
  End = (4840,12260,3600)
  FilletRadius = 0
  Length = 3600
  MakeFace = true
  Points = (2) [(4840,12260,0),(4840,12260,3600)]
  Start = (4840,12260,0)
  Subdivisions = 0
FEATURE [Part::Part2DObjectPython] Line  label="C5_GF_CenterLine"  # Draft 2D object (typed FeaturePython)
  Area = 0
  ChamferSize = 0
  Closed = false
  End = (4840,10,3600)
  FilletRadius = 0
  Length = 3600
  MakeFace = true
  Points = (2) [(4840,10,0),(4840,10,3600)]
  Start = (4840,10,0)
  Subdivisions = 0
FEATURE [Part::Part2DObjectPython] C65X65_20T25_C042  label="C65X65-20T25_C042"  # Draft 2D object (typed FeaturePython)
  Height = 650
  Width = 650
FEATURE [Part::FeaturePython] Structure001  label="C6_GF"  # Arch/BIM 24 (typed FeaturePython)
  AttacherType = Attacher::AttachEngine3D
  AttachmentOffset = pos=(0,0,0) rot=(0,0,1;1.5708rad)
  Base = -> C65X65_20T25_C042
  FaceMaker = 0
  Height = 3600
  HorizontalArea = 422500
  IfcData = attributes={"GlobalId": {"name": "GlobalId", "type": "IfcGloballyUniqueId", "is_enum": false, "enum_values": []}, "Description": {"... (+438 chars omitted),+1 more (map truncated)
  IfcType = 24
  Length = 0
  MapMode = 7
  MoveBase = false
  MoveWithHost = false
  Nodes = (2) [(4840,12260,0),(4840,12260,3600)]
  NodesOffset = 0
  Normal = (0,0,0)
  PerimeterLength = 2600
  Placement = pos=(4840,12260,0) rot=(0,0,1;1.5708rad)
  PredefinedType = 0
  Support = -> [Line001]
  VerticalArea = 9.36e+06
  Width = 100
  combos_load = ANGULAR-11 Max=4356.8422, -184219.33, -54091.08,ANGULAR-21 Max=4525.8677, -242931.44, -61790.84,ANGULAR-22 Max=4517.8194, -242937.62, -61786.97,+77 more (map truncated)
FEATURE [Part::FeaturePython] Structure  label="C5_GF"  # Arch/BIM 24 (typed FeaturePython)
  AttacherType = Attacher::AttachEngine3D
  AttachmentOffset = pos=(0,0,0) rot=(0,0,1;1.5708rad)
  Base = -> C65X65_20T25_C042
  FaceMaker = 0
  Height = 3600
  HorizontalArea = 422500
  IfcData = attributes={"GlobalId": {"name": "GlobalId", "type": "IfcGloballyUniqueId", "is_enum": false, "enum_values": []}, "Description": {"... (+438 chars omitted),+1 more (map truncated)
  IfcType = 24
  Length = 0
  MapMode = 7
  MoveBase = false
  MoveWithHost = false
  Nodes = (2) [(4840,10,0),(4840,10,3600)]
  NodesOffset = 0
  Normal = (0,0,0)
  PerimeterLength = 2600
  Placement = pos=(4840,10,0) rot=(0,0,1;1.5708rad)
  PredefinedType = 0
  Support = -> [Line]
  VerticalArea = 9.36e+06
  Width = 100
  combos_load = ANGULAR-11 Max=4367.8534, 131971.28, -31044.87,ANGULAR-21 Max=4536.1225, 172230.33, -32244.67,ANGULAR-22 Max=4528.0191, 172226.11, -32236.45,+77 more (map truncated)
FEATURE [Part::Part2DObjectPython] C60X65_14T20_C041  label="C60X65-14T20_C041"  # Draft 2D object (typed FeaturePython)
  Height = 650
  Width = 600
FEATURE [Part::Part2DObjectPython] Line002  label="C7_GF_CenterLine"  # Draft 2D object (typed FeaturePython)
  Area = 0
  ChamferSize = 0
  Closed = false
  End = (21480,12260,3600)
  FilletRadius = 0
  Length = 3600
  MakeFace = true
  Points = (2) [(21480,12260,0),(21480,12260,3600)]
  Start = (21480,12260,0)
  Subdivisions = 0
FEATURE [Part::FeaturePython] Structure002  label="C7_GF"  # Arch/BIM 24 (typed FeaturePython)
  AttacherType = Attacher::AttachEngine3D
  AttachmentOffset = pos=(0,0,0) rot=(0,0,1;1.5708rad)
  Base = -> C60X65_14T20_C041
  FaceMaker = 0
  Height = 3600
  HorizontalArea = 390000
  IfcData = attributes={"GlobalId": {"name": "GlobalId", "type": "IfcGloballyUniqueId", "is_enum": false, "enum_values": []}, "Description": {"... (+438 chars omitted),+1 more (map truncated)
  IfcType = 24
  Length = 0
  MapMode = 7
  MoveBase = false
  MoveWithHost = false
  Nodes = (2) [(21480,12260,0),(21480,12260,3600)]
  NodesOffset = 0
  Normal = (0,0,0)
  PerimeterLength = 2500
  Placement = pos=(21480,12260,0) rot=(0,0,1;1.5708rad)
  PredefinedType = 0
  Support = -> [Line002]
  VerticalArea = 9e+06
  Width = 100
  combos_load = ANGULAR-11 Max=2816.6105, -22433.34, 7057.06,ANGULAR-21 Max=2843.5494, -28034.07, 8691.86,ANGULAR-22 Max=2838.7314, -28043.78, 8687.24,+77 more (map truncated)
FEATURE [Part::Part2DObjectPython] Line004  label="C2_GF_CenterLine"  # Draft 2D object (typed FeaturePython)
  Area = 0
  ChamferSize = 0
  Closed = false
  End = (13320,12260,3600)
  FilletRadius = 0
  Length = 3600
  MakeFace = true
  Points = (2) [(13320,12260,0),(13320,12260,3600)]
  Start = (13320,12260,0)
  Subdivisions = 0
FEATURE [Part::Part2DObjectPython] C65X65_16T25_C042  label="C65X65-16T25_C042"  # Draft 2D object (typed FeaturePython)
  Height = 650
  Width = 650
FEATURE [Part::Part2DObjectPython] Line003  label="C1_GF_CenterLine"  # Draft 2D object (typed FeaturePython)
  Area = 0
  ChamferSize = 0
  Closed = false
  End = (9720,12260,3600)
  FilletRadius = 0
  Length = 3600
  MakeFace = true
  Points = (2) [(9720,12260,0),(9720,12260,3600)]
  Start = (9720,12260,0)
  Subdivisions = 0
FEATURE [Part::FeaturePython] Structure003  label="C1_GF"  # Arch/BIM 24 (typed FeaturePython)
  AttacherType = Attacher::AttachEngine3D
  AttachmentOffset = pos=(0,0,0) rot=(0,0,1;1.5708rad)
  Base = -> C65X65_16T25_C042
  FaceMaker = 0
  Height = 3600
  HorizontalArea = 422500
  IfcData = attributes={"GlobalId": {"name": "GlobalId", "type": "IfcGloballyUniqueId", "is_enum": false, "enum_values": []}, "Description": {"... (+438 chars omitted),+1 more (map truncated)
  IfcType = 24
  Length = 0
  MapMode = 7
  MoveBase = false
  MoveWithHost = false
  Nodes = (2) [(9720,12260,0),(9720,12260,3600)]
  NodesOffset = 0
  Normal = (0,0,0)
  PerimeterLength = 2600
  Placement = pos=(9720,12260,0) rot=(0,0,1;1.5708rad)
  PredefinedType = 0
  Support = -> [Line003]
  VerticalArea = 9.36e+06
  Width = 100
  combos_load = ANGULAR-11 Max=3257.4219, -139103.36, -12698.53,ANGULAR-21 Max=3430.7131, -182700.78, -20106.65,ANGULAR-22 Max=3424.2552, -182711.28, -20114.19,+77 more (map truncated)
FEATURE [Part::FeaturePython] Structure004  label="C2_GF"  # Arch/BIM 24 (typed FeaturePython)
  AttacherType = Attacher::AttachEngine3D
  AttachmentOffset = pos=(0,0,0) rot=(0,0,1;1.5708rad)
  Base = -> C65X65_16T20_C042
  FaceMaker = 0
  Height = 3600
  HorizontalArea = 422500
  IfcData = attributes={"GlobalId": {"name": "GlobalId", "type": "IfcGloballyUniqueId", "is_enum": false, "enum_values": []}, "Description": {"... (+438 chars omitted),+1 more (map truncated)
  IfcType = 24
  Length = 0
  MapMode = 7
  MoveBase = false
  MoveWithHost = false
  Nodes = (2) [(13320,12260,0),(13320,12260,3600)]
  NodesOffset = 0
  Normal = (0,0,0)
  PerimeterLength = 2600
  Placement = pos=(13320,12260,0) rot=(0,0,1;1.5708rad)
  PredefinedType = 0
  Support = -> [Line004]
  VerticalArea = 9.36e+06
  Width = 100
  combos_load = ANGULAR-11 Max=2983.3951, -50654.44, -23801.41,ANGULAR-21 Max=3178.0419, -86570.96, -29067.29,ANGULAR-22 Max=3171.8194, -86580.72, -29071.52,+77 more (map truncated)
FEATURE [Part::Part2DObjectPython] Line006  label="C9_GF_CenterLine"  # Draft 2D object (typed FeaturePython)
  Area = 0
  ChamferSize = 0
  Closed = false
  End = (22140,10,3600)
  FilletRadius = 0
  Length = 3600
  MakeFace = true
  Points = (2) [(22140,10,0),(22140,10,3600)]
  Start = (22140,10,0)
  Subdivisions = 0
FEATURE [Part::Part2DObjectPython] C55X55_12T25_C042  label="C55X55-12T25_C042"  # Draft 2D object (typed FeaturePython)
  Height = 550
  Width = 550
FEATURE [Part::Part2DObjectPython] Line007  label="C11_GF_CenterLine"  # Draft 2D object (typed FeaturePython)
  Area = 0
  ChamferSize = 0
  Closed = false
  End = (21970,4110,3600)
  FilletRadius = 0
  Length = 3600
  MakeFace = true
  Points = (2) [(21970,4110,0),(21970,4110,3600)]
  Start = (21970,4110,0)
  Subdivisions = 0
FEATURE [Part::FeaturePython] Structure007  label="C11_GF"  # Arch/BIM 24 (typed FeaturePython)
  AttacherType = Attacher::AttachEngine3D
  AttachmentOffset = pos=(0,0,0) rot=(0,0,1;1.5708rad)
  Base = -> C55X55_12T25_C042
  FaceMaker = 0
  Height = 3600
  HorizontalArea = 302500
  IfcData = attributes={"GlobalId": {"name": "GlobalId", "type": "IfcGloballyUniqueId", "is_enum": false, "enum_values": []}, "Description": {"... (+438 chars omitted),+1 more (map truncated)
  IfcType = 24
  Length = 0
  MapMode = 7
  MoveBase = false
  MoveWithHost = false
  Nodes = (2) [(21970,4110,0),(21970,4110,3600)]
  NodesOffset = 0
  Normal = (0,0,0)
  PerimeterLength = 2200
  Placement = pos=(21970,4110,0) rot=(0,0,1;1.5708rad)
  PredefinedType = 0
  Support = -> [Line007]
  VerticalArea = 7.92e+06
  Width = 100
  combos_load = ANGULAR-11 Max=216.7641, 20078.13, 12922.84,ANGULAR-21 Max=238.9962, 7269.05, 15513.86,ANGULAR-22 Max=238.9911, 7264.08, 15514.64,+77 more (map truncated)
FEATURE [Part::Part2DObjectPython] Line005  label="C8_GF_CenterLine"  # Draft 2D object (typed FeaturePython)
  Area = 0
  ChamferSize = 0
  Closed = false
  End = (17400,12260,3600)
  FilletRadius = 0
  Length = 3600
  MakeFace = true
  Points = (2) [(17400,12260,0),(17400,12260,3600)]
  Start = (17400,12260,0)
  Subdivisions = 0
FEATURE [Part::FeaturePython] Structure005  label="C8_GF"  # Arch/BIM 24 (typed FeaturePython)
  AttacherType = Attacher::AttachEngine3D
  AttachmentOffset = pos=(0,0,0) rot=(0,0,1;1.5708rad)
  Base = -> C65X65_16T20_C042
  FaceMaker = 0
  Height = 3600
  HorizontalArea = 422500
  IfcData = attributes={"GlobalId": {"name": "GlobalId", "type": "IfcGloballyUniqueId", "is_enum": false, "enum_values": []}, "Description": {"... (+438 chars omitted),+1 more (map truncated)
  IfcType = 24
  Length = 0
  MapMode = 7
  MoveBase = false
  MoveWithHost = false
  Nodes = (2) [(17400,12260,0),(17400,12260,3600)]
  NodesOffset = 0
  Normal = (0,0,0)
  PerimeterLength = 2600
  Placement = pos=(17400,12260,0) rot=(0,0,1;1.5708rad)
  PredefinedType = 0
  Support = -> [Line005]
  VerticalArea = 9.36e+06
  Width = 100
  combos_load = ANGULAR-11 Max=2865.7798, -60550.67, -41219.69,ANGULAR-21 Max=3078.1149, -103227.64, -54690.6,ANGULAR-22 Max=3071.9531, -103239.13, -54695.37,+77 more (map truncated)
FEATURE [Part::FeaturePython] Structure006  label="C9_GF"  # Arch/BIM 24 (typed FeaturePython)
  AttacherType = Attacher::AttachEngine3D
  AttachmentOffset = pos=(0,0,0) rot=(0,0,1;1.5708rad)
  Base = -> C60X65_14T20_C041
  FaceMaker = 0
  Height = 3600
  HorizontalArea = 390000
  IfcData = attributes={"GlobalId": {"name": "GlobalId", "type": "IfcGloballyUniqueId", "is_enum": false, "enum_values": []}, "Description": {"... (+438 chars omitted),+1 more (map truncated)
  IfcType = 24
  Length = 0
  MapMode = 7
  MoveBase = false
  MoveWithHost = false
  Nodes = (2) [(22140,10,0),(22140,10,3600)]
  NodesOffset = 0
  Normal = (0,0,0)
  PerimeterLength = 2500
  Placement = pos=(22140,10,0) rot=(0,0,1;1.5708rad)
  PredefinedType = 0
  Support = -> [Line006]
  VerticalArea = 9e+06
  Width = 100
  combos_load = ANGULAR-11 Max=2831.1902, -32400.05, -1157.66,ANGULAR-21 Max=2858.2201, -35789.94, -3268.54,ANGULAR-22 Max=2853.2068, -35795.35, -3268.5,+77 more (map truncated)
FEATURE [Part::Part2DObjectPython] Line009  label="C3_GF_CenterLine"  # Draft 2D object (typed FeaturePython)
  Area = 0
  ChamferSize = 0
  Closed = false
  End = (9720,10,3600)
  FilletRadius = 0
  Length = 3600
  MakeFace = true
  Points = (2) [(9720,10,0),(9720,10,3600)]
  Start = (9720,10,0)
  Subdivisions = 0
FEATURE [Part::FeaturePython] Structure009  label="C3_GF"  # Arch/BIM 24 (typed FeaturePython)
  AttacherType = Attacher::AttachEngine3D
  AttachmentOffset = pos=(0,0,0) rot=(0,0,1;1.5708rad)
  Base = -> C65X65_16T25_C042
  FaceMaker = 0
  Height = 3600
  HorizontalArea = 422500
  IfcData = attributes={"GlobalId": {"name": "GlobalId", "type": "IfcGloballyUniqueId", "is_enum": false, "enum_values": []}, "Description": {"... (+438 chars omitted),+1 more (map truncated)
  IfcType = 24
  Length = 0
  MapMode = 7
  MoveBase = false
  MoveWithHost = false
  Nodes = (2) [(9720,10,0),(9720,10,3600)]
  NodesOffset = 0
  Normal = (0,0,0)
  PerimeterLength = 2600
  Placement = pos=(9720,10,0) rot=(0,0,1;1.5708rad)
  PredefinedType = 0
  Support = -> [Line009]
  VerticalArea = 9.36e+06
  Width = 100
  combos_load = ANGULAR-11 Max=3477.8285, 49358.85, 23416.11,ANGULAR-21 Max=3724.8303, 61264.01, 27495.41,ANGULAR-22 Max=3717.9708, 61263.86, 27490.74,+77 more (map truncated)
FEATURE [Part::Part2DObjectPython] Line010  label="C4_GF_CenterLine"  # Draft 2D object (typed FeaturePython)
  Area = 0
  ChamferSize = 0
  Closed = false
  End = (13320,10,3600)
  FilletRadius = 0
  Length = 3600
  MakeFace = true
  Points = (2) [(13320,10,0),(13320,10,3600)]
  Start = (13320,10,0)
  Subdivisions = 0
FEATURE [Part::FeaturePython] Structure010  label="C4_GF"  # Arch/BIM 24 (typed FeaturePython)
  AttacherType = Attacher::AttachEngine3D
  AttachmentOffset = pos=(0,0,0) rot=(0,0,1;1.5708rad)
  Base = -> C65X65_16T20_C042
  FaceMaker = 0
  Height = 3600
  HorizontalArea = 422500
  IfcData = attributes={"GlobalId": {"name": "GlobalId", "type": "IfcGloballyUniqueId", "is_enum": false, "enum_values": []}, "Description": {"... (+438 chars omitted),+1 more (map truncated)
  IfcType = 24
  Length = 0
  MapMode = 7
  MoveBase = false
  MoveWithHost = false
  Nodes = (2) [(13320,10,0),(13320,10,3600)]
  NodesOffset = 0
  Normal = (0,0,0)
  PerimeterLength = 2600
  Placement = pos=(13320,10,0) rot=(0,0,1;1.5708rad)
  PredefinedType = 0
  Support = -> [Line010]
  VerticalArea = 9.36e+06
  Width = 100
  combos_load = ANGULAR-11 Max=3145.6593, 99041.57, -12991.76,ANGULAR-21 Max=3384.0657, 144156.94, -14197.18,ANGULAR-22 Max=3377.5533, 144145.03, -14197.11,+77 more (map truncated)
FEATURE [Part::Part2DObjectPython] Line008  label="C12_GF_CenterLine"  # Draft 2D object (typed FeaturePython)
  Area = 0
  ChamferSize = 0
  Closed = false
  End = (17400,4110,3600)
  FilletRadius = 0
  Length = 3600
  MakeFace = true
  Points = (2) [(17400,4110,0),(17400,4110,3600)]
  Start = (17400,4110,0)
  Subdivisions = 0
FEATURE [Part::FeaturePython] Structure008  label="C12_GF"  # Arch/BIM 24 (typed FeaturePython)
  AttacherType = Attacher::AttachEngine3D
  AttachmentOffset = pos=(0,0,0) rot=(0,0,1;1.5708rad)
  Base = -> C55X55_12T25_C042
  FaceMaker = 0
  Height = 3600
  HorizontalArea = 302500
  IfcData = attributes={"GlobalId": {"name": "GlobalId", "type": "IfcGloballyUniqueId", "is_enum": false, "enum_values": []}, "Description": {"... (+438 chars omitted),+1 more (map truncated)
  IfcType = 24
  Length = 0
  MapMode = 7
  MoveBase = false
  MoveWithHost = false
  Nodes = (2) [(17400,4110,0),(17400,4110,3600)]
  NodesOffset = 0
  Normal = (0,0,0)
  PerimeterLength = 2200
  Placement = pos=(17400,4110,0) rot=(0,0,1;1.5708rad)
  PredefinedType = 0
  Support = -> [Line008]
  VerticalArea = 7.92e+06
  Width = 100
  combos_load = ANGULAR-11 Max=359.26, 56694.55, -43371.85,ANGULAR-21 Max=495.8163, 82328.2, -54586.87,ANGULAR-22 Max=495.797, 82329.4, -54585.09,+77 more (map truncated)
FEATURE [Part::Part2DObjectPython] C55X55_20T25_C042  label="C55X55-20T25_C042"  # Draft 2D object (typed FeaturePython)
  Height = 550
  Width = 550
FEATURE [Part::Part2DObjectPython] Line013  label="C14_GF_CenterLine"  # Draft 2D object (typed FeaturePython)
  Area = 0
  ChamferSize = 0
  Closed = false
  End = (10,10,3600)
  FilletRadius = 0
  Length = 3600
  MakeFace = true
  Points = (2) [(10,10,0),(10,10,3600)]
  Start = (10,10,0)
  Subdivisions = 0
FEATURE [Part::Part2DObjectPython] Line012  label="C13_GF_CenterLine"  # Draft 2D object (typed FeaturePython)
  Area = 0
  ChamferSize = 0
  Closed = false
  End = (13320,4110,3600)
  FilletRadius = 0
  Length = 3600
  MakeFace = true
  Points = (2) [(13320,4110,0),(13320,4110,3600)]
  Start = (13320,4110,0)
  Subdivisions = 0
FEATURE [Part::FeaturePython] Structure012  label="C13_GF"  # Arch/BIM 24 (typed FeaturePython)
  AttacherType = Attacher::AttachEngine3D
  AttachmentOffset = pos=(0,0,0) rot=(0,0,1;1.5708rad)
  Base = -> C55X55_12T25_C042
  FaceMaker = 0
  Height = 3600
  HorizontalArea = 302500
  IfcData = attributes={"GlobalId": {"name": "GlobalId", "type": "IfcGloballyUniqueId", "is_enum": false, "enum_values": []}, "Description": {"... (+438 chars omitted),+1 more (map truncated)
  IfcType = 24
  Length = 0
  MapMode = 7
  MoveBase = false
  MoveWithHost = false
  Nodes = (2) [(13320,4110,0),(13320,4110,3600)]
  NodesOffset = 0
  Normal = (0,0,0)
  PerimeterLength = 2200
  Placement = pos=(13320,4110,0) rot=(0,0,1;1.5708rad)
  PredefinedType = 0
  Support = -> [Line012]
  VerticalArea = 7.92e+06
  Width = 100
  combos_load = ANGULAR-11 Max=364.4398, 66201.54, 48448.42,ANGULAR-21 Max=481.6183, 91050.26, 62289.28,ANGULAR-22 Max=481.5912, 91045.18, 62281.42,+77 more (map truncated)
FEATURE [Part::Part2DObjectPython] Line011  label="C10_GF_CenterLine"  # Draft 2D object (typed FeaturePython)
  Area = 0
  ChamferSize = 0
  Closed = false
  End = (17400,10,3600)
  FilletRadius = 0
  Length = 3600
  MakeFace = true
  Points = (2) [(17400,10,0),(17400,10,3600)]
  Start = (17400,10,0)
  Subdivisions = 0
FEATURE [Part::FeaturePython] Structure011  label="C10_GF"  # Arch/BIM 24 (typed FeaturePython)
  AttacherType = Attacher::AttachEngine3D
  AttachmentOffset = pos=(0,0,0) rot=(0,0,1;1.5708rad)
  Base = -> C65X65_16T25_C042
  FaceMaker = 0
  Height = 3600
  HorizontalArea = 422500
  IfcData = attributes={"GlobalId": {"name": "GlobalId", "type": "IfcGloballyUniqueId", "is_enum": false, "enum_values": []}, "Description": {"... (+438 chars omitted),+1 more (map truncated)
  IfcType = 24
  Length = 0
  MapMode = 7
  MoveBase = false
  MoveWithHost = false
  Nodes = (2) [(17400,10,0),(17400,10,3600)]
  NodesOffset = 0
  Normal = (0,0,0)
  PerimeterLength = 2600
  Placement = pos=(17400,10,0) rot=(0,0,1;1.5708rad)
  PredefinedType = 0
  Support = -> [Line011]
  VerticalArea = 9.36e+06
  Width = 100
  combos_load = ANGULAR-11 Max=2835.862, 44074.44, -16464.94,ANGULAR-21 Max=3009.4862, 78731.78, -17465.36,ANGULAR-22 Max=3003.1654, 78732.66, -17465.36,+77 more (map truncated)
FEATURE [Part::Part2DObjectPython] BOX10X012  # Draft 2D object (typed FeaturePython)
  Height = 100
  Thickness = 4
  Width = 100
FEATURE [Part::FeaturePython] Structure013  label="C14_GF"  # Arch/BIM 24 (typed FeaturePython)
  AttacherType = Attacher::AttachEngine3D
  AttachmentOffset = pos=(0,0,0) rot=(0,0,1;1.5708rad)
  Base = -> C55X55_20T25_C042
  FaceMaker = 0
  Height = 3600
  HorizontalArea = 302500
  IfcData = attributes={"GlobalId": {"name": "GlobalId", "type": "IfcGloballyUniqueId", "is_enum": false, "enum_values": []}, "Description": {"... (+438 chars omitted),+1 more (map truncated)
  IfcType = 24
  Length = 0
  MapMode = 7
  MoveBase = false
  MoveWithHost = false
  Nodes = (2) [(10,10,0),(10,10,3600)]
  NodesOffset = 0
  Normal = (0,0,0)
  PerimeterLength = 2200
  Placement = pos=(10,10,0) rot=(0,0,1;1.5708rad)
  PredefinedType = 0
  Support = -> [Line013]
  VerticalArea = 7.92e+06
  Width = 100
  combos_load = ANGULAR-11 Max=319.3581, 212575.9, -32581.85,ANGULAR-21 Max=344.9917, 243740.98, -32189.0,ANGULAR-22 Max=344.979, 243738.9, -32173.84,+77 more (map truncated)
FEATURE [Part::Part2DObjectPython] Line015  label="C16_GF_CenterLine"  # Draft 2D object (typed FeaturePython)
  Area = 0
  ChamferSize = 0
  Closed = false
  End = (11790,9340,3600)
  FilletRadius = 0
  Length = 3600
  MakeFace = true
  Points = (2) [(11790,9340,0),(11790,9340,3600)]
  Start = (11790,9340,0)
  Subdivisions = 0
FEATURE [Part::Part2DObjectPython] Line014  label="C15_GF_CenterLine"  # Draft 2D object (typed FeaturePython)
  Area = 0
  ChamferSize = 0
  Closed = false
  End = (10,12260,3600)
  FilletRadius = 0
  Length = 3600
  MakeFace = true
  Points = (2) [(10,12260,0),(10,12260,3600)]
  Start = (10,12260,0)
  Subdivisions = 0
FEATURE [Part::FeaturePython] Structure014  label="C15_GF"  # Arch/BIM 24 (typed FeaturePython)
  AttacherType = Attacher::AttachEngine3D
  AttachmentOffset = pos=(0,0,0) rot=(0,0,1;1.5708rad)
  Base = -> C55X55_20T25_C042
  FaceMaker = 0
  Height = 3600
  HorizontalArea = 302500
  IfcData = attributes={"GlobalId": {"name": "GlobalId", "type": "IfcGloballyUniqueId", "is_enum": false, "enum_values": []}, "Description": {"... (+438 chars omitted),+1 more (map truncated)
  IfcType = 24
  Length = 0
  MapMode = 7
  MoveBase = false
  MoveWithHost = false
  Nodes = (2) [(10,12260,0),(10,12260,3600)]
  NodesOffset = 0
  Normal = (0,0,0)
  PerimeterLength = 2200
  Placement = pos=(10,12260,0) rot=(0,0,1;1.5708rad)
  PredefinedType = 0
  Support = -> [Line014]
  VerticalArea = 7.92e+06
  Width = 100
  combos_load = ANGULAR-11 Max=320.2916, -224719.46, -38434.52,ANGULAR-21 Max=346.3422, -259856.1, -40168.06,ANGULAR-22 Max=346.3302, -259858.25, -40155.1,+77 more (map truncated)
FEATURE [Part::FeaturePython] Structure015  label="C16_GF"  # Arch/BIM 24 (typed FeaturePython)
  AttacherType = Attacher::AttachEngine3D
  AttachmentOffset = pos=(0,0,0) rot=(0,0,1;1.5708rad)
  Base = -> BOX10X012
  FaceMaker = 0
  Height = 3600
  HorizontalArea = 1536
  IfcData = attributes={"GlobalId": {"name": "GlobalId", "type": "IfcGloballyUniqueId", "is_enum": false, "enum_values": []}, "Description": {"... (+438 chars omitted),+1 more (map truncated)
  IfcType = 24
  Length = 0
  MapMode = 7
  MoveBase = false
  MoveWithHost = false
  Nodes = (2) [(11790,9340,0),(11790,9340,3600)]
  NodesOffset = 0
  Normal = (0,0,0)
  PerimeterLength = 400
  Placement = pos=(11790,9340,0) rot=(0,0,1;1.5708rad)
  PredefinedType = 0
  Support = -> [Line015]
  VerticalArea = 2.7648e+06
  Width = 100
FEATURE [App::DocumentObjectGroup] Columns001
  Group = -> [Structure,Structure001,Structure002,Structure003,Structure004,Structure005,Structure006,Structure007,Structure008,Structure009,Structure010,Structure011,Structure012,Structure013,Structure014,Structure015]
FEATURE [App::FeaturePython] Text  # WARN: FeaturePython — macro-defined, semantics opaque (R4)
  Placement = pos=(4840,12640,3600) rot=(0,0,1;0rad)
  Text = Edge 3 | 1.55
FEATURE [Part::FeaturePython] Punch  # WARN: FeaturePython — macro-defined, semantics opaque (R4)
  Area = 2809125
  Av = 400
  Fys = 340000
  I22 = 4.92495e+11
  I23 = 3.00249e+11
  I33 = 1.15606e+12
  Location = 6
  Ratio = 1.55
  Use_Reinforcement = true
  Vc = 3.84655e+09
  Vs = 4.09391e+09
  Vu = 5955345000
  alpha_s = 30
  angle = 0
  b0 = 3405
  bx = 650
  by = 650
  center_of_column = (4840,12260,0)
  center_of_load = (4840,12260,0)
  center_of_punch = (4900.9,11887.2,-412.5)
  column = -> Structure001
  combos_ratio = ANGULAR-11=1.51,ANGULAR-21=1.55,ANGULAR-22=1.55,ANGULAR-31=1.40,ANGULAR-32=1.39,ANGULAR-41=1.39,ANGULAR-42=1.38,ANGULAR-51=1.53,ANGULAR-510=1.53,+36 more (map truncated)
  d = 825
  fc = 30000
  foundation = -> Foundation
  gamma_vx = 0.4
  gamma_vy = 0.4
  id = C6_GF
  one_way_shear_capacity = 1.92328e+09
  s = 27.4066
  text = -> Text
  user_location = false
  vc = 1369.31
  x = 2104.56
FEATURE [App::FeaturePython] Text001  # WARN: FeaturePython — macro-defined, semantics opaque (R4)
  Placement = pos=(21868.9,12093.8,3600) rot=(0,0,1;0rad)
  Text = Corner 3 | 2.21
FEATURE [Part::FeaturePython] Punch001  # WARN: FeaturePython — macro-defined, semantics opaque (R4)
  Area = 1.83059e+06
  Av = 400
  Fys = 340000
  I22 = 2.77294e+11
  I23 = 0
  I33 = 2.96088e+11
  Location = 2
  Ratio = 2.21
  Use_Reinforcement = true
  Vc = 2.50664e+09
  Vs = 4.86453e+09
  Vu = 5.52838e+09
  alpha_s = 20
  angle = 0
  b0 = 2218.9
  bx = 650
  by = 600
  center_of_column = (21480,12260,0)
  center_of_load = (21480,12260,0)
  center_of_punch = (21028.4,11816.5,-412.5)
  column = -> Structure002
  combos_ratio = ANGULAR-11=1.84,ANGULAR-21=1.86,ANGULAR-22=1.85,ANGULAR-31=1.70,ANGULAR-32=1.69,ANGULAR-41=1.68,ANGULAR-42=1.68,ANGULAR-51=2.17,ANGULAR-510=2.16,+36 more (map truncated)
  d = 825
  fc = 30000
  foundation = -> Foundation
  gamma_vx = 0.390434
  gamma_vy = 0.409642
  id = C7_GF
  one_way_shear_capacity = 1.25332e+09
  s = 23.0649
  text = -> Text001
  user_location = false
  vc = 1369.31
  x = 4260.7
FEATURE [App::FeaturePython] Text002  # WARN: FeaturePython — macro-defined, semantics opaque (R4)
  Placement = pos=(4840,-370,3600) rot=(0,0,1;0rad)
  Text = Edge 1 | 2.04
FEATURE [Part::FeaturePython] Punch002  # WARN: FeaturePython — macro-defined, semantics opaque (R4)
  Area = 2809125
  Av = 400
  Fys = 340000
  I22 = 4.92495e+11
  I23 = 3.00249e+11
  I33 = 1.15606e+12
  Location = 4
  Ratio = 2.04
  Use_Reinforcement = true
  Vc = 3.84655e+09
  Vs = 6.64085e+09
  Vu = 7.86555e+09
  alpha_s = 30
  angle = 0
  b0 = 3405
  bx = 650
  by = 650
  center_of_column = (4840,10,0)
  center_of_load = (4840,10,0)
  center_of_punch = (4900.9,382.771,-412.5)
  column = -> Structure
  combos_ratio = ANGULAR-11=1.60,ANGULAR-21=1.65,ANGULAR-22=1.64,ANGULAR-31=1.50,ANGULAR-32=1.48,ANGULAR-41=1.48,ANGULAR-42=1.47,ANGULAR-51=1.88,ANGULAR-510=1.88,+36 more (map truncated)
  d = 825
  fc = 30000
  foundation = -> Foundation
  gamma_vx = 0.4
  gamma_vy = 0.4
  id = C5_GF
  one_way_shear_capacity = 1.92328e+09
  s = 16.8954
  text = -> Text002
  user_location = false
  vc = 1369.31
  x = 2911.92
FEATURE [App::FeaturePython] Text003  # WARN: FeaturePython — macro-defined, semantics opaque (R4)
  Placement = pos=(9720,12640,3600) rot=(0,0,1;0rad)
  Text = Edge 3 | 1.12
FEATURE [Part::FeaturePython] Punch003  # WARN: FeaturePython — macro-defined, semantics opaque (R4)
  Area = 3060750
  Av = 400
  Fys = 340000
  I22 = 5.25337e+11
  I23 = 3.02085e+11
  I33 = 1.29254e+12
  Location = 6
  Ratio = 1.12
  Use_Reinforcement = true
  Vc = 4.1911e+09
  Vs = 2.05283e+09
  Vu = 4682947500
  alpha_s = 30
  angle = 0
  b0 = 3710
  bx = 650
  by = 650
  center_of_column = (9720,12260,0)
  center_of_load = (9720,12260,0)
  center_of_punch = (9720,11859.1,-412.5)
  column = -> Structure003
  combos_ratio = ANGULAR-11=1.07,ANGULAR-21=1.12,ANGULAR-22=1.12,ANGULAR-31=1.02,ANGULAR-32=1.01,ANGULAR-41=1.00,ANGULAR-42=1.00,ANGULAR-51=1.08,ANGULAR-510=1.07,+36 more (map truncated)
  d = 825
  fc = 30000
  foundation = -> Foundation
  gamma_vx = 0.4
  gamma_vy = 0.4
  id = C1_GF
  one_way_shear_capacity = 2.09555e+09
  s = 54.6564
  text = -> Text003
  user_location = false
  vc = 1369.31
  x = 1566.77
FEATURE [App::FeaturePython] Text004  # WARN: FeaturePython — macro-defined, semantics opaque (R4)
  Placement = pos=(13320,12640,3600) rot=(0,0,1;0rad)
  Text = Edge 3 | 1.05
FEATURE [Part::FeaturePython] Punch004  # WARN: FeaturePython — macro-defined, semantics opaque (R4)
  Area = 3060750
  Av = 400
  Fys = 340000
  I22 = 5.25337e+11
  I23 = 3.02085e+11
  I33 = 1.29254e+12
  Location = 6
  Ratio = 1.05
  Use_Reinforcement = true
  Vc = 4.1911e+09
  Vs = 1.68554e+09
  Vu = 4407480000
  alpha_s = 30
  angle = 0
  b0 = 3710
  bx = 650
  by = 650
  center_of_column = (13320,12260,0)
  center_of_load = (13320,12260,0)
  center_of_punch = (13320,11859.1,-412.5)
  column = -> Structure004
  combos_ratio = ANGULAR-11=0.99,ANGULAR-21=1.05,ANGULAR-22=1.05,ANGULAR-31=0.96,ANGULAR-32=0.95,ANGULAR-41=0.94,ANGULAR-42=0.93,ANGULAR-51=0.94,ANGULAR-510=0.94,+36 more (map truncated)
  d = 825
  fc = 30000
  foundation = -> Foundation
  gamma_vx = 0.4
  gamma_vy = 0.4
  id = C2_GF
  one_way_shear_capacity = 2.09555e+09
  s = 66.5664
  text = -> Text004
  user_location = false
  vc = 1369.31
  x = 1450.35
FEATURE [App::FeaturePython] Text005  # WARN: FeaturePython — macro-defined, semantics opaque (R4)
  Placement = pos=(22306.7,4110,3600) rot=(0,0,1;0rad)
  Text = Edge 2 | 0.23
FEATURE [Part::FeaturePython] Punch005  # WARN: FeaturePython — macro-defined, semantics opaque (R4)
  Area = 2.46594e+06
  Av = 400
  Fys = 340000
  I22 = 9.05287e+11
  I23 = 2.28292e+11
  I33 = 3.59901e+11
  Location = 5
  Ratio = 0.23
  Use_Reinforcement = false
  Vc = 3.37663e+09
  Vs = 0
  Vu = 7.64442e+08
  alpha_s = 30
  angle = 0
  b0 = 2989.02
  bx = 550
  by = 550
  center_of_column = (21970,4110,0)
  center_of_load = (21970,4110,0)
  center_of_punch = (21608.9,4156.76,-412.5)
  column = -> Structure007
  combos_ratio = ANGULAR-11=0.09,ANGULAR-21=0.10,ANGULAR-22=0.10,ANGULAR-31=0.09,ANGULAR-32=0.09,ANGULAR-41=0.09,ANGULAR-42=0.09,ANGULAR-51=0.17,ANGULAR-510=0.18,+36 more (map truncated)
  d = 825
  fc = 30000
  foundation = -> Foundation
  gamma_vx = 0.4
  gamma_vy = 0.4
  id = C11_GF
  one_way_shear_capacity = 1.68831e+09
  s = 0
  text = -> Text005
  user_location = false
  vc = 1369.31
  x = 0
FEATURE [App::FeaturePython] Text006  # WARN: FeaturePython — macro-defined, semantics opaque (R4)
  Placement = pos=(17400,12640,3600) rot=(0,0,1;0rad)
  Text = Edge 3 | 1.01
FEATURE [Part::FeaturePython] Punch006  # WARN: FeaturePython — macro-defined, semantics opaque (R4)
  Area = 3060750
  Av = 400
  Fys = 340000
  I22 = 5.25337e+11
  I23 = 3.02085e+11
  I33 = 1.29254e+12
  Location = 6
  Ratio = 1.01
  Use_Reinforcement = true
  Vc = 4.1911e+09
  Vs = 1.44068e+09
  Vu = 4223835000
  alpha_s = 30
  angle = 0
  b0 = 3710
  bx = 650
  by = 650
  center_of_column = (17400,12260,0)
  center_of_load = (17400,12260,0)
  center_of_punch = (17400,11859.1,-412.5)
  column = -> Structure005
  combos_ratio = ANGULAR-11=0.95,ANGULAR-21=1.01,ANGULAR-22=1.01,ANGULAR-31=0.91,ANGULAR-32=0.90,ANGULAR-41=0.89,ANGULAR-42=0.88,ANGULAR-51=0.97,ANGULAR-510=0.97,+36 more (map truncated)
  d = 825
  fc = 30000
  foundation = -> Foundation
  gamma_vx = 0.4
  gamma_vy = 0.4
  id = C8_GF
  one_way_shear_capacity = 2.09555e+09
  s = 77.8801
  text = -> Text006
  user_location = false
  vc = 1369.31
  x = 1372.73
FEATURE [App::FeaturePython] Text007  # WARN: FeaturePython — macro-defined, semantics opaque (R4)
  Placement = pos=(22465,176.25,3600) rot=(0,0,1;0rad)
  Text = Corner 2 | 2.35
FEATURE [Part::FeaturePython] Punch007  # WARN: FeaturePython — macro-defined, semantics opaque (R4)
  Area = 1.76725e+06
  Av = 400
  Fys = 340000
  I22 = 2.72548e+11
  I23 = 0
  I33 = 2.50253e+11
  Location = 1
  Ratio = 2.35
  Use_Reinforcement = true
  Vc = 2.41991e+09
  Vs = 5.16748e+09
  Vu = 5.69054e+09
  Warnings = Vs > 2 * Vc
  alpha_s = 20
  angle = 0
  b0 = 2142.12
  bx = 650
  by = 600
  center_of_column = (22140,10,0)
  center_of_load = (22140,10,0)
  center_of_punch = (21659.7,443.908,-412.5)
  column = -> Structure006
  combos_ratio = ANGULAR-11=1.94,ANGULAR-21=1.96,ANGULAR-22=1.96,ANGULAR-31=1.79,ANGULAR-32=1.78,ANGULAR-41=1.77,ANGULAR-42=1.77,ANGULAR-51=2.19,ANGULAR-510=2.21,+36 more (map truncated)
  d = 825
  fc = 30000
  foundation = -> Foundation
  gamma_vx = 0.390434
  gamma_vy = 0.409642
  id = C9_GF
  one_way_shear_capacity = 1.20995e+09
  s = 21.7127
  text = -> Text007
  user_location = false
  vc = 1369.31
  x = 4397.78
FEATURE [App::FeaturePython] Text009  # WARN: FeaturePython — macro-defined, semantics opaque (R4)
  Placement = pos=(9720,-370,3600) rot=(0,0,1;0rad)
  Text = Edge 1 | 1.56
FEATURE [Part::FeaturePython] Punch009  # WARN: FeaturePython — macro-defined, semantics opaque (R4)
  Area = 3.06075e+06
  Av = 400
  Fys = 340000
  I22 = 5.25337e+11
  I23 = 3.02085e+11
  I33 = 1.29254e+12
  Location = 4
  Ratio = 1.56
  Use_Reinforcement = true
  Vc = 4.1911e+09
  Vs = 4.54224e+09
  Vu = 6.55e+09
  alpha_s = 30
  angle = 0
  b0 = 3710
  bx = 650
  by = 650
  center_of_column = (9720,10,0)
  center_of_load = (9720,10,0)
  center_of_punch = (9720,410.895,-412.5)
  column = -> Structure009
  combos_ratio = ANGULAR-11=1.17,ANGULAR-21=1.25,ANGULAR-22=1.24,ANGULAR-31=1.13,ANGULAR-32=1.12,ANGULAR-41=1.12,ANGULAR-42=1.12,ANGULAR-51=1.42,ANGULAR-510=1.43,+36 more (map truncated)
  d = 825
  fc = 30000
  foundation = -> Foundation
  gamma_vx = 0.4
  gamma_vy = 0.4
  id = C3_GF
  one_way_shear_capacity = 2.09555e+09
  s = 24.7015
  text = -> Text009
  user_location = false
  vc = 1369.31
  x = 2355.9
FEATURE [App::FeaturePython] Text010  # WARN: FeaturePython — macro-defined, semantics opaque (R4)
  Placement = pos=(13320,-370,3600) rot=(0,0,1;0rad)
  Text = Edge 1 | 1.42
FEATURE [Part::FeaturePython] Punch010  # WARN: FeaturePython — macro-defined, semantics opaque (R4)
  Area = 3.06075e+06
  Av = 400
  Fys = 340000
  I22 = 5.25337e+11
  I23 = 3.02085e+11
  I33 = 1.29254e+12
  Location = 4
  Ratio = 1.42
  Use_Reinforcement = true
  Vc = 4.1911e+09
  Vs = 3.72604e+09
  Vu = 5.93785e+09
  alpha_s = 30
  angle = 0
  b0 = 3710
  bx = 650
  by = 650
  center_of_column = (13320,10,0)
  center_of_load = (13320,10,0)
  center_of_punch = (13320,410.895,-412.5)
  column = -> Structure010
  combos_ratio = ANGULAR-11=1.05,ANGULAR-21=1.12,ANGULAR-22=1.12,ANGULAR-31=1.02,ANGULAR-32=1.01,ANGULAR-41=1.00,ANGULAR-42=1.00,ANGULAR-51=1.20,ANGULAR-510=1.23,+36 more (map truncated)
  d = 825
  fc = 30000
  foundation = -> Foundation
  gamma_vx = 0.4
  gamma_vy = 0.4
  id = C4_GF
  one_way_shear_capacity = 2.09555e+09
  s = 30.1124
  text = -> Text010
  user_location = false
  vc = 1369.31
  x = 2097.17
FEATURE [App::FeaturePython] Text011  # WARN: FeaturePython — macro-defined, semantics opaque (R4)
  Placement = pos=(12760,4110,3600) rot=(0,0,1;0rad)
  Text = Edge 4 | 0.31
FEATURE [Part::FeaturePython] Punch011  # WARN: FeaturePython — macro-defined, semantics opaque (R4)
  Area = 2.2275e+06
  Av = 400
  Fys = 340000
  I22 = 8.36219e+11
  I23 = 2.19838e+11
  I33 = 4.70109e+11
  Location = 7
  Ratio = 0.31
  Use_Reinforcement = false
  Vc = 3.05013e+09
  Vs = 0
  Vu = 9.57825e+08
  alpha_s = 30
  angle = 0
  b0 = 2700
  bx = 550
  by = 550
  center_of_column = (13320,4110,0)
  center_of_load = (13320,4110,0)
  center_of_punch = (13453.8,4110,-412.5)
  column = -> Structure012
  combos_ratio = ANGULAR-11=0.14,ANGULAR-21=0.18,ANGULAR-22=0.18,ANGULAR-31=0.16,ANGULAR-32=0.16,ANGULAR-41=0.16,ANGULAR-42=0.16,ANGULAR-51=0.25,ANGULAR-510=0.26,+36 more (map truncated)
  d = 825
  fc = 30000
  foundation = -> Foundation
  gamma_vx = 0.4
  gamma_vy = 0.4
  id = C13_GF
  one_way_shear_capacity = 1.52506e+09
  s = 0
  text = -> Text011
  user_location = false
  vc = 1369.31
  x = 0
FEATURE [App::FeaturePython] Text012  # WARN: FeaturePython — macro-defined, semantics opaque (R4)
  Placement = pos=(17400,-370,3600) rot=(0,0,1;0rad)
  Text = Edge 1 | 1.32
FEATURE [Part::FeaturePython] Punch012  # WARN: FeaturePython — macro-defined, semantics opaque (R4)
  Area = 3.06075e+06
  Av = 400
  Fys = 340000
  I22 = 5.25337e+11
  I23 = 3.02085e+11
  I33 = 1.29254e+12
  Location = 4
  Ratio = 1.32
  Use_Reinforcement = true
  Vc = 4.1911e+09
  Vs = 3.19551e+09
  Vu = 5.53996e+09
  alpha_s = 30
  angle = 0
  b0 = 3710
  bx = 650
  by = 650
  center_of_column = (17400,10,0)
  center_of_load = (17400,10,0)
  center_of_punch = (17400,410.895,-412.5)
  column = -> Structure011
  combos_ratio = ANGULAR-11=0.96,ANGULAR-21=1.01,ANGULAR-22=1.01,ANGULAR-31=0.91,ANGULAR-32=0.90,ANGULAR-41=0.89,ANGULAR-42=0.88,ANGULAR-51=1.07,ANGULAR-510=1.10,+36 more (map truncated)
  d = 825
  fc = 30000
  foundation = -> Foundation
  gamma_vx = 0.4
  gamma_vy = 0.4
  id = C10_GF
  one_way_shear_capacity = 2.09555e+09
  s = 35.1118
  text = -> Text012
  user_location = false
  vc = 1369.31
  x = 1929
FEATURE [App::FeaturePython] Text013  # WARN: FeaturePython — macro-defined, semantics opaque (R4)
  Placement = pos=(-270,12106.2,3600) rot=(0,0,1;0rad)
  Text = Corner 4 | 0.34
FEATURE [Part::FeaturePython] Punch013  # WARN: FeaturePython — macro-defined, semantics opaque (R4)
  Area = 1.4025e+06
  Av = 400
  Fys = 340000
  I22 = 2.24947e+11
  I23 = 0
  I33 = 1.85868e+11
  Location = 3
  Ratio = 0.34
  Use_Reinforcement = false
  Vc = 1.92045e+09
  Vs = 0
  Vu = 6.4515e+08
  alpha_s = 20
  angle = 0
  b0 = 1700
  bx = 550
  by = 550
  center_of_column = (10,12260,0)
  center_of_load = (10,12260,0)
  center_of_punch = (443.235,11906.3,-412.5)
  column = -> Structure014
  combos_ratio = ANGULAR-11=0.20,ANGULAR-21=0.21,ANGULAR-22=0.21,ANGULAR-31=0.20,ANGULAR-32=0.20,ANGULAR-41=0.20,ANGULAR-42=0.20,ANGULAR-51=0.34,ANGULAR-510=0.33,+36 more (map truncated)
  d = 825
  fc = 30000
  foundation = -> Foundation
  gamma_vx = 0.4
  gamma_vy = 0.4
  id = C15_GF
  one_way_shear_capacity = 9.60226e+08
  s = 0
  text = -> Text013
  user_location = false
  vc = 1369.31
  x = 0
FEATURE [App::FeaturePython] Text014  # WARN: FeaturePython — macro-defined, semantics opaque (R4)
  Placement = pos=(-270,163.75,3600) rot=(0,0,1;0rad)
  Text = Corner 1 | 0.46
FEATURE [Part::FeaturePython] Punch014  # WARN: FeaturePython — macro-defined, semantics opaque (R4)
  Area = 1.4025e+06
  Av = 400
  Fys = 340000
  I22 = 2.24947e+11
  I23 = 0
  I33 = 1.85868e+11
  Location = 0
  Ratio = 0.46
  Use_Reinforcement = false
  Vc = 1.92045e+09
  Vs = 0
  Vu = 8.83575e+08
  alpha_s = 20
  angle = 0
  b0 = 1700
  bx = 550
  by = 550
  center_of_column = (10,10,0)
  center_of_load = (10,10,0)
  center_of_punch = (443.235,363.676,-412.5)
  column = -> Structure013
  combos_ratio = ANGULAR-11=0.20,ANGULAR-21=0.21,ANGULAR-22=0.21,ANGULAR-31=0.20,ANGULAR-32=0.20,ANGULAR-41=0.20,ANGULAR-42=0.20,ANGULAR-51=0.39,ANGULAR-510=0.39,+36 more (map truncated)
  d = 825
  fc = 30000
  foundation = -> Foundation
  gamma_vx = 0.4
  gamma_vy = 0.4
  id = C14_GF
  one_way_shear_capacity = 9.60226e+08
  s = 0
  text = -> Text014
  user_location = false
  vc = 1369.31
  x = 0
FEATURE [App::DocumentObjectGroup] Punches
  Group = -> [Punch,Punch001,Punch002,Punch003,Punch004,Punch005,Punch006,Punch007,Punch009,Punch010,Punch011,Punch012,Punch013,Punch014]
note: 4 file-system paths scrubbed to <path> (originals preserved in the JSON sidecar)
